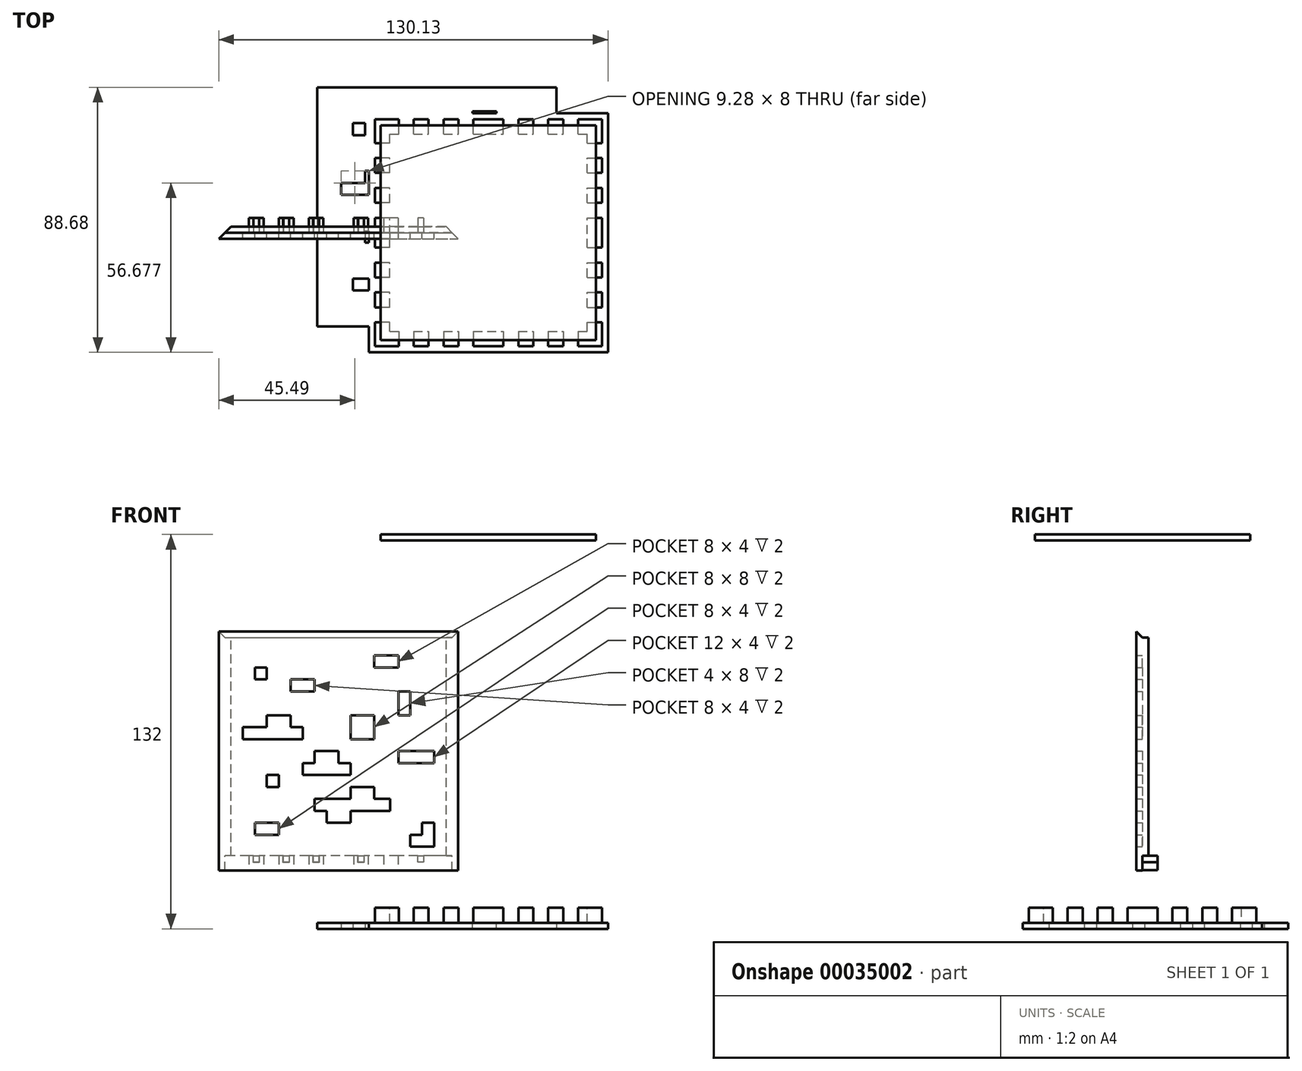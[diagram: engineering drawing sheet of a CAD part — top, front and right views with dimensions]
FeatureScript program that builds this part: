
annotation { "Feature Type Name" : "Feature", "Feature Type Description" : "" }
export const myFeature = defineFeature(function(context is Context, id is Id, definition is map)
    precondition{}
    {
        {
            var Q0;
            Q0=qCreatedBy(makeId("Top.planeOp"),FACE);
            var sketch = newSketch(context, id + "F0", { "sketchPlane" : qUnion([Q0])});
            skLineSegment(sketch, "E0", {"start": v(-57.28, 48.68) * mm, "end": v(-57.28, -31.32) * mm});
            skLineSegment(sketch, "E1.1.0.0", {"start": v(-53.28, 48.68) * mm, "end": v(-53.28, -31.32) * mm, "construction": true});
            skLineSegment(sketch, "E1.2.0.0", {"start": v(-49.28, 48.68) * mm, "end": v(-49.28, -31.32) * mm, "construction": true});
            skLineSegment(sketch, "E1.3.0.0", {"start": v(-45.28, 48.68) * mm, "end": v(-45.28, -31.32) * mm, "construction": true});
            skLineSegment(sketch, "E1.4.0.0", {"start": v(-41.28, 48.68) * mm, "end": v(-41.28, -31.32) * mm, "construction": true});
            skLineSegment(sketch, "E1.5.0.0", {"start": v(-37.28, 48.68) * mm, "end": v(-37.28, -31.32) * mm, "construction": true});
            skLineSegment(sketch, "E1.6.0.0", {"start": v(-33.28, 48.68) * mm, "end": v(-33.28, -31.32) * mm, "construction": true});
            skLineSegment(sketch, "E1.7.0.0", {"start": v(-29.28, 48.68) * mm, "end": v(-29.28, -31.32) * mm, "construction": true});
            skLineSegment(sketch, "E1.8.0.0", {"start": v(-25.28, 48.68) * mm, "end": v(-25.28, -31.32) * mm, "construction": true});
            skLineSegment(sketch, "E1.9.0.0", {"start": v(-21.28, 48.68) * mm, "end": v(-21.28, -31.32) * mm, "construction": true});
            skLineSegment(sketch, "E1.10.0.0", {"start": v(-17.28, 48.68) * mm, "end": v(-17.28, -31.32) * mm, "construction": true});
            skLineSegment(sketch, "E1.11.0.0", {"start": v(-13.28, 48.68) * mm, "end": v(-13.28, -31.32) * mm, "construction": true});
            skLineSegment(sketch, "E1.12.0.0", {"start": v(-9.28, 48.68) * mm, "end": v(-9.28, -31.32) * mm, "construction": true});
            skLineSegment(sketch, "E1.13.0.0", {"start": v(-5.28, 48.68) * mm, "end": v(-5.28, -31.32) * mm, "construction": true});
            skLineSegment(sketch, "E1.14.0.0", {"start": v(-1.28, 48.68) * mm, "end": v(-1.28, -31.32) * mm, "construction": true});
            skLineSegment(sketch, "E1.15.0.0", {"start": v(2.72, 48.68) * mm, "end": v(2.72, -31.32) * mm, "construction": true});
            skLineSegment(sketch, "E1.16.0.0", {"start": v(6.72, 48.68) * mm, "end": v(6.72, -31.32) * mm, "construction": true});
            skLineSegment(sketch, "E1.17.0.0", {"start": v(10.72, 48.68) * mm, "end": v(10.72, -31.32) * mm, "construction": true});
            skLineSegment(sketch, "E1.18.0.0", {"start": v(14.72, 48.68) * mm, "end": v(14.72, -31.32) * mm, "construction": true});
            skLineSegment(sketch, "E1.19.0.0", {"start": v(18.72, 48.68) * mm, "end": v(18.72, -31.32) * mm, "construction": true});
            skLineSegment(sketch, "E1.direction1", {"start": v(-57.28, -31.32) * mm, "end": v(-53.28, -31.32) * mm, "construction": true});
            skLineSegment(sketch, "E2", {"start": v(-57.28, 48.68) * mm, "end": v(22.72, 48.68) * mm});
            skLineSegment(sketch, "E3.0.20.0", {"start": v(22.72, 48.68) * mm, "end": v(22.72, -31.32) * mm});
            skLineSegment(sketch, "E4.0.1.0", {"start": v(-57.28, 44.68) * mm, "end": v(22.72, 44.68) * mm, "construction": true});
            skLineSegment(sketch, "E4.0.2.0", {"start": v(-57.28, 40.68) * mm, "end": v(22.72, 40.68) * mm, "construction": true});
            skLineSegment(sketch, "E4.0.3.0", {"start": v(-57.28, 36.68) * mm, "end": v(22.72, 36.68) * mm, "construction": true});
            skLineSegment(sketch, "E4.0.4.0", {"start": v(-57.28, 32.68) * mm, "end": v(22.72, 32.68) * mm, "construction": true});
            skLineSegment(sketch, "E4.0.5.0", {"start": v(-57.28, 28.68) * mm, "end": v(22.72, 28.68) * mm, "construction": true});
            skLineSegment(sketch, "E4.0.6.0", {"start": v(-57.28, 24.68) * mm, "end": v(22.72, 24.68) * mm, "construction": true});
            skLineSegment(sketch, "E4.0.7.0", {"start": v(-57.28, 20.68) * mm, "end": v(22.72, 20.68) * mm, "construction": true});
            skLineSegment(sketch, "E4.0.8.0", {"start": v(-57.28, 16.68) * mm, "end": v(22.72, 16.68) * mm, "construction": true});
            skLineSegment(sketch, "E4.0.9.0", {"start": v(-57.28, 12.68) * mm, "end": v(22.72, 12.68) * mm, "construction": true});
            skLineSegment(sketch, "E4.0.10.0", {"start": v(-57.28, 8.68) * mm, "end": v(22.72, 8.68) * mm, "construction": true});
            skLineSegment(sketch, "E4.0.11.0", {"start": v(-57.28, 4.68) * mm, "end": v(22.72, 4.68) * mm, "construction": true});
            skLineSegment(sketch, "E4.0.12.0", {"start": v(-57.28, 0.68) * mm, "end": v(22.72, 0.68) * mm, "construction": true});
            skLineSegment(sketch, "E4.0.13.0", {"start": v(-57.28, -3.32) * mm, "end": v(22.72, -3.32) * mm, "construction": true});
            skLineSegment(sketch, "E4.0.14.0", {"start": v(-57.28, -7.32) * mm, "end": v(22.72, -7.32) * mm, "construction": true});
            skLineSegment(sketch, "E4.0.15.0", {"start": v(-57.28, -11.32) * mm, "end": v(22.72, -11.32) * mm, "construction": true});
            skLineSegment(sketch, "E4.0.16.0", {"start": v(-57.28, -15.32) * mm, "end": v(22.72, -15.32) * mm, "construction": true});
            skLineSegment(sketch, "E4.0.17.0", {"start": v(-57.28, -19.32) * mm, "end": v(22.72, -19.32) * mm, "construction": true});
            skLineSegment(sketch, "E4.0.18.0", {"start": v(-57.28, -23.32) * mm, "end": v(22.72, -23.32) * mm, "construction": true});
            skLineSegment(sketch, "E4.0.19.0", {"start": v(-57.28, -27.32) * mm, "end": v(22.72, -27.32) * mm, "construction": true});
            skLineSegment(sketch, "E4.0.20.0", {"start": v(-57.28, -31.32) * mm, "end": v(22.72, -31.32) * mm});
            skLineSegment(sketch, "E4.direction1", {"start": v(-57.28, 48.68) * mm, "end": v(-53.28, 48.68) * mm, "construction": true});
            skLineSegment(sketch, "E4.direction2", {"start": v(-57.28, 48.68) * mm, "end": v(-57.28, 44.68) * mm, "construction": true});
            skLineSegment(sketch, "E5.bottom", {"start": v(-45.28, 36.68) * mm, "end": v(-41.28, 36.68) * mm});
            skLineSegment(sketch, "E5.top", {"start": v(-45.28, 32.68) * mm, "end": v(-41.28, 32.68) * mm});
            skLineSegment(sketch, "E5.left", {"start": v(-45.28, 36.68) * mm, "end": v(-45.28, 32.68) * mm});
            skLineSegment(sketch, "E5.right", {"start": v(-41.28, 36.68) * mm, "end": v(-41.28, 32.68) * mm});
            skLineSegment(sketch, "E6.bottom", {"start": v(-33.28, 32.68) * mm, "end": v(-25.28, 32.68) * mm});
            skLineSegment(sketch, "E6.top", {"start": v(-33.28, 28.68) * mm, "end": v(-25.28, 28.68) * mm});
            skLineSegment(sketch, "E6.left", {"start": v(-33.28, 32.68) * mm, "end": v(-33.28, 28.68) * mm});
            skLineSegment(sketch, "E6.right", {"start": v(-25.28, 32.68) * mm, "end": v(-25.28, 28.68) * mm});
            skLineSegment(sketch, "E7.bottom", {"start": v(-5.28, 36.68) * mm, "end": v(2.72, 36.68) * mm});
            skLineSegment(sketch, "E7.top", {"start": v(-5.28, 40.68) * mm, "end": v(2.72, 40.68) * mm});
            skLineSegment(sketch, "E7.left", {"start": v(-5.28, 36.68) * mm, "end": v(-5.28, 40.68) * mm});
            skLineSegment(sketch, "E7.right", {"start": v(2.72, 36.68) * mm, "end": v(2.72, 40.68) * mm});
            skPoint(sketch, "E8.firstSnap0", {"position": v(-17.28, 20.68) * mm});
            skLineSegment(sketch, "E8.bottom", {"start": v(-41.28, 20.68) * mm, "end": v(-33.28, 20.68) * mm});
            skLineSegment(sketch, "E8.top", {"start": v(-41.28, 16.68) * mm, "end": v(-33.28, 16.68) * mm});
            skLineSegment(sketch, "E8.left", {"start": v(-41.28, 20.68) * mm, "end": v(-41.28, 16.68) * mm});
            skLineSegment(sketch, "E8.right", {"start": v(-33.28, 20.68) * mm, "end": v(-33.28, 16.68) * mm});
            skLineSegment(sketch, "E9.bottom", {"start": v(-49.28, 16.68) * mm, "end": v(-29.28, 16.68) * mm});
            skLineSegment(sketch, "E9.top", {"start": v(-49.28, 12.68) * mm, "end": v(-29.28, 12.68) * mm});
            skLineSegment(sketch, "E9.left", {"start": v(-49.28, 16.68) * mm, "end": v(-49.28, 12.68) * mm});
            skLineSegment(sketch, "E9.right", {"start": v(-29.28, 16.68) * mm, "end": v(-29.28, 12.68) * mm});
            skLineSegment(sketch, "E10.bottom", {"start": v(-25.28, 8.68) * mm, "end": v(-17.28, 8.68) * mm});
            skLineSegment(sketch, "E10.top", {"start": v(-25.28, 4.68) * mm, "end": v(-17.28, 4.68) * mm});
            skLineSegment(sketch, "E10.left", {"start": v(-25.28, 8.68) * mm, "end": v(-25.28, 4.68) * mm});
            skLineSegment(sketch, "E10.right", {"start": v(-17.28, 8.68) * mm, "end": v(-17.28, 4.68) * mm});
            skLineSegment(sketch, "E11.bottom", {"start": v(-29.28, 4.68) * mm, "end": v(-13.28, 4.68) * mm});
            skLineSegment(sketch, "E11.top", {"start": v(-29.28, 0.68) * mm, "end": v(-13.28, 0.68) * mm});
            skLineSegment(sketch, "E11.left", {"start": v(-29.28, 4.68) * mm, "end": v(-29.28, 0.68) * mm});
            skLineSegment(sketch, "E11.right", {"start": v(-13.28, 4.68) * mm, "end": v(-13.28, 0.68) * mm});
            skLineSegment(sketch, "E12.bottom", {"start": v(-41.28, 0.68) * mm, "end": v(-37.28, 0.68) * mm});
            skLineSegment(sketch, "E12.top", {"start": v(-41.28, -3.32) * mm, "end": v(-37.28, -3.32) * mm});
            skLineSegment(sketch, "E12.left", {"start": v(-41.28, 0.68) * mm, "end": v(-41.28, -3.32) * mm});
            skLineSegment(sketch, "E12.right", {"start": v(-37.28, 0.68) * mm, "end": v(-37.28, -3.32) * mm});
            skLineSegment(sketch, "E13.bottom", {"start": v(-13.28, 12.68) * mm, "end": v(-5.28, 12.68) * mm});
            skLineSegment(sketch, "E13.top", {"start": v(-13.28, 20.68) * mm, "end": v(-5.28, 20.68) * mm});
            skLineSegment(sketch, "E13.left", {"start": v(-13.28, 12.68) * mm, "end": v(-13.28, 20.68) * mm});
            skLineSegment(sketch, "E13.right", {"start": v(-5.28, 12.68) * mm, "end": v(-5.28, 20.68) * mm});
            skLineSegment(sketch, "E14.bottom", {"start": v(2.72, 28.68) * mm, "end": v(6.72, 28.68) * mm});
            skLineSegment(sketch, "E14.top", {"start": v(2.72, 20.68) * mm, "end": v(6.72, 20.68) * mm});
            skLineSegment(sketch, "E14.left", {"start": v(2.72, 28.68) * mm, "end": v(2.72, 20.68) * mm});
            skLineSegment(sketch, "E14.right", {"start": v(6.72, 28.68) * mm, "end": v(6.72, 20.68) * mm});
            skLineSegment(sketch, "E15.bottom", {"start": v(-13.28, -3.32) * mm, "end": v(-5.28, -3.32) * mm});
            skLineSegment(sketch, "E15.top", {"start": v(-13.28, -7.32) * mm, "end": v(-5.28, -7.32) * mm});
            skLineSegment(sketch, "E15.left", {"start": v(-13.28, -3.32) * mm, "end": v(-13.28, -7.32) * mm});
            skLineSegment(sketch, "E15.right", {"start": v(-5.28, -3.32) * mm, "end": v(-5.28, -7.32) * mm});
            skLineSegment(sketch, "E16.bottom", {"start": v(0, -7.32) * mm, "end": v(-25.28, -7.32) * mm});
            skLineSegment(sketch, "E16.top", {"start": v(0, -11.32) * mm, "end": v(-25.28, -11.32) * mm});
            skLineSegment(sketch, "E16.left", {"start": v(0, -7.32) * mm, "end": v(0, -11.32) * mm});
            skLineSegment(sketch, "E16.right", {"start": v(-25.28, -7.32) * mm, "end": v(-25.28, -11.32) * mm});
            skLineSegment(sketch, "E17.bottom", {"start": v(-21.28, -11.32) * mm, "end": v(-13.28, -11.32) * mm});
            skLineSegment(sketch, "E17.top", {"start": v(-21.28, -15.32) * mm, "end": v(-13.28, -15.32) * mm});
            skLineSegment(sketch, "E17.left", {"start": v(-21.28, -11.32) * mm, "end": v(-21.28, -15.32) * mm});
            skLineSegment(sketch, "E17.right", {"start": v(-13.28, -11.32) * mm, "end": v(-13.28, -15.32) * mm});
            skLineSegment(sketch, "E18.bottom", {"start": v(-37.28, -15.32) * mm, "end": v(-45.28, -15.32) * mm});
            skLineSegment(sketch, "E18.top", {"start": v(-37.28, -19.32) * mm, "end": v(-45.28, -19.32) * mm});
            skLineSegment(sketch, "E18.left", {"start": v(-37.28, -15.32) * mm, "end": v(-37.28, -19.32) * mm});
            skLineSegment(sketch, "E18.right", {"start": v(-45.28, -15.32) * mm, "end": v(-45.28, -19.32) * mm});
            skLineSegment(sketch, "E19.bottom", {"start": v(6.72, -23.32) * mm, "end": v(14.72, -23.32) * mm});
            skLineSegment(sketch, "E19.top", {"start": v(6.72, -19.32) * mm, "end": v(14.72, -19.32) * mm});
            skLineSegment(sketch, "E19.left", {"start": v(6.72, -23.32) * mm, "end": v(6.72, -19.32) * mm});
            skLineSegment(sketch, "E19.right", {"start": v(14.72, -23.32) * mm, "end": v(14.72, -19.32) * mm});
            skLineSegment(sketch, "E20.bottom", {"start": v(10.72, -15.32) * mm, "end": v(14.72, -15.32) * mm});
            skLineSegment(sketch, "E20.top", {"start": v(10.72, -19.32) * mm, "end": v(14.72, -19.32) * mm});
            skLineSegment(sketch, "E20.left", {"start": v(10.72, -15.32) * mm, "end": v(10.72, -19.32) * mm});
            skLineSegment(sketch, "E20.right", {"start": v(14.72, -15.32) * mm, "end": v(14.72, -19.32) * mm});
            skLineSegment(sketch, "E21.bottom", {"start": v(2.72, 4.68) * mm, "end": v(14.72, 4.68) * mm});
            skLineSegment(sketch, "E21.top", {"start": v(2.72, 8.68) * mm, "end": v(14.72, 8.68) * mm});
            skLineSegment(sketch, "E21.left", {"start": v(2.72, 4.68) * mm, "end": v(2.72, 8.68) * mm});
            skLineSegment(sketch, "E21.right", {"start": v(14.72, 4.68) * mm, "end": v(14.72, 8.68) * mm});
            skSolve(sketch);
        }
        {
            var Q0;
            Q0=makeQuery(id+"F0.imprint","IMPRINT",FACE,{"disambiguationData":[TD([[makeQuery(id+"F0.imprint","IMPRINT",EDGE,{"derivedFrom":sQuery(id+"F0.wireOp",EDGE,"E0")}),1.0]])]});
            extrude(context, id + "F1", {"entities" : qUnion([Q0]), "depth" : 2 * mm});
        }
        {
            var Q0;
            Q0=qCreatedBy(makeId("Top.planeOp"),FACE);
            var sketch = newSketch(context, id + "F2", { "sketchPlane" : qUnion([Q0])});
            skLineSegment(sketch, "E22.bottom", {"start": v(40, 40) * mm, "end": v(-40, 40) * mm});
            skLineSegment(sketch, "E22.top", {"start": v(40, -40) * mm, "end": v(-40, -40) * mm});
            skLineSegment(sketch, "E22.left", {"start": v(40, 40) * mm, "end": v(40, -40) * mm});
            skLineSegment(sketch, "E22.right", {"start": v(-40, 40) * mm, "end": v(-40, -40) * mm});
            skPoint(sketch, "E22.middle", {"position": v(0, 0) * mm});
            skSolve(sketch);
        }
        {
            var Q0;
            Q0=makeQuery(id+"F2.imprint","IMPRINT",FACE,{"disambiguationData":[TD([[makeQuery(id+"F2.imprint","IMPRINT",EDGE,{"derivedFrom":sQuery(id+"F2.wireOp",EDGE,"E22.bottom")}),1.0]])]});
            extrude(context, id + "F3", {"entities" : qUnion([Q0]), "depth" : 2 * mm});
        }
        {
            var Q0;
            Q0=makeQuery(id+"F3.opExtrude","CAP_FACE",FACE,{"disambiguationData":[OSD([sQuery(id+"F2.wireOp",EDGE,"E22.bottom"),sQuery(id+"F2.wireOp",EDGE,"E22.top"),sQuery(id+"F2.wireOp",EDGE,"E22.left"),sQuery(id+"F2.wireOp",EDGE,"E22.right")])],"isStart":false});
            var sketch = newSketch(context, id + "F4", { "sketchPlane" : qUnion([Q0])});
            skLineSegment(sketch, "E23.bottom", {"start": v(38, 38) * mm, "end": v(-38, 38) * mm});
            skLineSegment(sketch, "E23.top", {"start": v(38, -38) * mm, "end": v(-38, -38) * mm});
            skLineSegment(sketch, "E23.left", {"start": v(38, 38) * mm, "end": v(38, -38) * mm});
            skLineSegment(sketch, "E23.right", {"start": v(-38, 38) * mm, "end": v(-38, -38) * mm});
            skPoint(sketch, "E23.middle", {"position": v(0, 0) * mm});
            skLineSegment(sketch, "E24.bottom", {"start": v(-33, -33) * mm, "end": v(33, -33) * mm});
            skLineSegment(sketch, "E24.top", {"start": v(-33, 33) * mm, "end": v(33, 33) * mm});
            skLineSegment(sketch, "E24.left", {"start": v(-33, -33) * mm, "end": v(-33, 33) * mm});
            skLineSegment(sketch, "E24.right", {"start": v(33, -33) * mm, "end": v(33, 33) * mm});
            skSolve(sketch);
        }
        {
            var Q0;
            Q0=makeQuery(id+"F4.imprint","IMPRINT",FACE,{"disambiguationData":[TD([[makeQuery(id+"F4.imprint","IMPRINT",EDGE,{"derivedFrom":sQuery(id+"F4.wireOp",EDGE,"E23.bottom")}),1.0]])]});
            extrude(context, id + "F5", {"entities" : qUnion([Q0]), "operationType" : NewBodyOperationType.ADD, "depth" : 5 * mm});
        }
        {
            var Q0;
            Q0=makeQuery(id+"F5.opExtrude","CAP_FACE",FACE,{"disambiguationData":[OSD([sQuery(id+"F4.wireOp",EDGE,"E23.bottom"),sQuery(id+"F4.wireOp",EDGE,"E23.top"),sQuery(id+"F4.wireOp",EDGE,"E23.left"),sQuery(id+"F4.wireOp",EDGE,"E23.right"),sQuery(id+"F4.wireOp",EDGE,"E24.bottom"),sQuery(id+"F4.wireOp",EDGE,"E24.top"),sQuery(id+"F4.wireOp",EDGE,"E24.left"),sQuery(id+"F4.wireOp",EDGE,"E24.right")])],"isStart":false});
            var sketch = newSketch(context, id + "F6", { "sketchPlane" : qUnion([Q0])});
            skLineSegment(sketch, "E25", {"start": v(-33, 30) * mm, "end": v(-38, 30) * mm});
            skLineSegment(sketch, "E26.0.1.0", {"start": v(-33, 25) * mm, "end": v(-38, 25) * mm});
            skLineSegment(sketch, "E26.0.2.0", {"start": v(-33, 20) * mm, "end": v(-38, 20) * mm});
            skLineSegment(sketch, "E26.0.3.0", {"start": v(-33, 15) * mm, "end": v(-38, 15) * mm});
            skLineSegment(sketch, "E26.0.4.0", {"start": v(-33, 10) * mm, "end": v(-38, 10) * mm});
            skLineSegment(sketch, "E26.0.5.0", {"start": v(-33, 5) * mm, "end": v(-38, 5) * mm});
            skLineSegment(sketch, "E26.0.6.0", {"start": v(-33, 0) * mm, "end": v(-38, 0) * mm});
            skLineSegment(sketch, "E26.direction1", {"start": v(-38, 30) * mm, "end": v(-13, 30) * mm, "construction": true});
            skLineSegment(sketch, "E26.direction2", {"start": v(-38, 30) * mm, "end": v(-38, 25) * mm, "construction": true});
            skLineSegment(sketch, "E27.0.0.7", {"start": v(-33, -5) * mm, "end": v(-38, -5) * mm});
            skLineSegment(sketch, "E27.0.0.8", {"start": v(-33, -10) * mm, "end": v(-38, -10) * mm});
            skLineSegment(sketch, "E27.0.0.9", {"start": v(-33, -15) * mm, "end": v(-38, -15) * mm});
            skLineSegment(sketch, "E27.0.0.10", {"start": v(-33, -20) * mm, "end": v(-38, -20) * mm});
            skLineSegment(sketch, "E27.0.0.11", {"start": v(-33, -25) * mm, "end": v(-38, -25) * mm});
            skLineSegment(sketch, "E28.0.0.12", {"start": v(-33, -30) * mm, "end": v(-38, -30) * mm});
            skLineSegment(sketch, "E29", {"start": v(0, 0) * mm, "end": v(0, 8.43) * mm, "construction": true});
            skLineSegment(sketch, "E30.MirrorCS", {"start": v(33, -30) * mm, "end": v(38, -30) * mm});
            skLineSegment(sketch, "E31.MirrorCS", {"start": v(33, -25) * mm, "end": v(38, -25) * mm});
            skLineSegment(sketch, "E32.MirrorCS", {"start": v(33, -20) * mm, "end": v(38, -20) * mm});
            skLineSegment(sketch, "E33.MirrorCS", {"start": v(33, -15) * mm, "end": v(38, -15) * mm});
            skLineSegment(sketch, "E34.MirrorCS", {"start": v(33, -10) * mm, "end": v(38, -10) * mm});
            skLineSegment(sketch, "E35.MirrorCS", {"start": v(33, -5) * mm, "end": v(38, -5) * mm});
            skLineSegment(sketch, "E36.MirrorCS", {"start": v(33, 0) * mm, "end": v(38, 0) * mm});
            skLineSegment(sketch, "E37.MirrorCS", {"start": v(33, 5) * mm, "end": v(38, 5) * mm});
            skLineSegment(sketch, "E38.MirrorCS", {"start": v(33, 10) * mm, "end": v(38, 10) * mm});
            skLineSegment(sketch, "E39.MirrorCS", {"start": v(33, 15) * mm, "end": v(38, 15) * mm});
            skLineSegment(sketch, "E40.MirrorCS", {"start": v(33, 20) * mm, "end": v(38, 20) * mm});
            skLineSegment(sketch, "E41.MirrorCS", {"start": v(33, 25) * mm, "end": v(38, 25) * mm});
            skLineSegment(sketch, "E42.MirrorCS", {"start": v(33, 30) * mm, "end": v(38, 30) * mm});
            skLineSegment(sketch, "E43", {"start": v(-30, -33) * mm, "end": v(-30, -38) * mm});
            skLineSegment(sketch, "E44.1.0.0", {"start": v(-25, -33) * mm, "end": v(-25, -38) * mm});
            skLineSegment(sketch, "E44.2.0.0", {"start": v(-20, -33) * mm, "end": v(-20, -38) * mm});
            skLineSegment(sketch, "E44.3.0.0", {"start": v(-15, -33) * mm, "end": v(-15, -38) * mm});
            skLineSegment(sketch, "E44.4.0.0", {"start": v(-10, -33) * mm, "end": v(-10, -38) * mm});
            skLineSegment(sketch, "E44.5.0.0", {"start": v(-5, -33) * mm, "end": v(-5, -38) * mm});
            skLineSegment(sketch, "E44.6.0.0", {"start": v(0, -33) * mm, "end": v(0, -38) * mm});
            skLineSegment(sketch, "E44.7.0.0", {"start": v(5, -33) * mm, "end": v(5, -38) * mm});
            skLineSegment(sketch, "E44.8.0.0", {"start": v(10, -33) * mm, "end": v(10, -38) * mm});
            skLineSegment(sketch, "E44.9.0.0", {"start": v(15, -33) * mm, "end": v(15, -38) * mm});
            skLineSegment(sketch, "E44.10.0.0", {"start": v(20, -33) * mm, "end": v(20, -38) * mm});
            skLineSegment(sketch, "E44.11.0.0", {"start": v(25, -33) * mm, "end": v(25, -38) * mm});
            skLineSegment(sketch, "E44.12.0.0", {"start": v(30, -33) * mm, "end": v(30, -38) * mm});
            skLineSegment(sketch, "E44.direction1", {"start": v(-30, -38) * mm, "end": v(-25, -38) * mm, "construction": true});
            skLineSegment(sketch, "E45", {"start": v(0, 0) * mm, "end": v(-14.9, 0) * mm, "construction": true});
            skLineSegment(sketch, "E46.MirrorCS", {"start": v(5, 33) * mm, "end": v(5, 38) * mm});
            skLineSegment(sketch, "E47.MirrorCS", {"start": v(-5, 33) * mm, "end": v(-5, 38) * mm});
            skLineSegment(sketch, "E48.MirrorCS", {"start": v(-15, 33) * mm, "end": v(-15, 38) * mm});
            skLineSegment(sketch, "E49.MirrorCS", {"start": v(0, 33) * mm, "end": v(0, 38) * mm});
            skLineSegment(sketch, "E50.MirrorCS", {"start": v(-10, 33) * mm, "end": v(-10, 38) * mm});
            skLineSegment(sketch, "E51.MirrorCS", {"start": v(-25, 33) * mm, "end": v(-25, 38) * mm});
            skLineSegment(sketch, "E52.MirrorCS", {"start": v(-30, 33) * mm, "end": v(-30, 38) * mm});
            skLineSegment(sketch, "E53.MirrorCS", {"start": v(-20, 33) * mm, "end": v(-20, 38) * mm});
            skLineSegment(sketch, "E54.MirrorCS", {"start": v(10, 33) * mm, "end": v(10, 38) * mm});
            skLineSegment(sketch, "E55.MirrorCS", {"start": v(20, 33) * mm, "end": v(20, 38) * mm});
            skLineSegment(sketch, "E56.MirrorCS", {"start": v(-30, 38) * mm, "end": v(-25, 38) * mm, "construction": true});
            skLineSegment(sketch, "E57.MirrorCS", {"start": v(25, 33) * mm, "end": v(25, 38) * mm});
            skLineSegment(sketch, "E58.MirrorCS", {"start": v(15, 33) * mm, "end": v(15, 38) * mm});
            skLineSegment(sketch, "E59.MirrorCS", {"start": v(30, 33) * mm, "end": v(30, 38) * mm});
            skSolve(sketch);
        }
        {
            var Q0;
            {var subQ0=sQuery(id+"F6.wireOp",EDGE,"E27.0.0.11");Q0=makeQuery(id+"F6.imprint","IMPRINT",FACE,{"disambiguationData":[TD([[makeQuery(id+"F6.imprint","IMPRINT",EDGE,{"derivedFrom":subQ0}),1.0]])]});}
            var Q1;
            {var subQ0=sQuery(id+"F6.wireOp",EDGE,"E27.0.0.9");Q1=makeQuery(id+"F6.imprint","IMPRINT",FACE,{"disambiguationData":[TD([[makeQuery(id+"F6.imprint","IMPRINT",EDGE,{"derivedFrom":subQ0}),1.0]])]});}
            var Q2;
            {var subQ0=sQuery(id+"F6.wireOp",EDGE,"E27.0.0.7");Q2=makeQuery(id+"F6.imprint","IMPRINT",FACE,{"disambiguationData":[TD([[makeQuery(id+"F6.imprint","IMPRINT",EDGE,{"derivedFrom":subQ0}),1.0]])]});}
            var Q3;
            {var subQ0=sQuery(id+"F6.wireOp",EDGE,"E25");Q3=makeQuery(id+"F6.imprint","IMPRINT",FACE,{"disambiguationData":[TD([[makeQuery(id+"F6.imprint","IMPRINT",EDGE,{"derivedFrom":subQ0}),1.0]])]});}
            var Q4;
            {var subQ0=sQuery(id+"F6.wireOp",EDGE,"E26.0.2.0");Q4=makeQuery(id+"F6.imprint","IMPRINT",FACE,{"disambiguationData":[TD([[makeQuery(id+"F6.imprint","IMPRINT",EDGE,{"derivedFrom":subQ0}),1.0]])]});}
            var Q5;
            {var subQ0=sQuery(id+"F6.wireOp",EDGE,"E26.0.4.0");Q5=makeQuery(id+"F6.imprint","IMPRINT",FACE,{"disambiguationData":[TD([[makeQuery(id+"F6.imprint","IMPRINT",EDGE,{"derivedFrom":subQ0}),1.0]])]});}
            var Q6;
            {var subQ0=sQuery(id+"F6.wireOp",EDGE,"E30.MirrorCS");Q6=makeQuery(id+"F6.imprint","IMPRINT",FACE,{"disambiguationData":[TD([[makeQuery(id+"F6.imprint","IMPRINT",EDGE,{"derivedFrom":subQ0}),1.0]])]});}
            var Q7;
            {var subQ0=sQuery(id+"F6.wireOp",EDGE,"E32.MirrorCS");Q7=makeQuery(id+"F6.imprint","IMPRINT",FACE,{"disambiguationData":[TD([[makeQuery(id+"F6.imprint","IMPRINT",EDGE,{"derivedFrom":subQ0}),1.0]])]});}
            var Q8;
            {var subQ0=sQuery(id+"F6.wireOp",EDGE,"E34.MirrorCS");Q8=makeQuery(id+"F6.imprint","IMPRINT",FACE,{"disambiguationData":[TD([[makeQuery(id+"F6.imprint","IMPRINT",EDGE,{"derivedFrom":subQ0}),1.0]])]});}
            var Q9;
            {var subQ0=sQuery(id+"F6.wireOp",EDGE,"E41.MirrorCS");Q9=makeQuery(id+"F6.imprint","IMPRINT",FACE,{"disambiguationData":[TD([[makeQuery(id+"F6.imprint","IMPRINT",EDGE,{"derivedFrom":subQ0}),1.0]])]});}
            var Q10;
            {var subQ0=sQuery(id+"F6.wireOp",EDGE,"E39.MirrorCS");Q10=makeQuery(id+"F6.imprint","IMPRINT",FACE,{"disambiguationData":[TD([[makeQuery(id+"F6.imprint","IMPRINT",EDGE,{"derivedFrom":subQ0}),1.0]])]});}
            var Q11;
            {var subQ0=sQuery(id+"F6.wireOp",EDGE,"E37.MirrorCS");Q11=makeQuery(id+"F6.imprint","IMPRINT",FACE,{"disambiguationData":[TD([[makeQuery(id+"F6.imprint","IMPRINT",EDGE,{"derivedFrom":subQ0}),1.0]])]});}
            var Q12;
            {var subQ0=sQuery(id+"F6.wireOp",EDGE,"E51.MirrorCS");Q12=makeQuery(id+"F6.imprint","IMPRINT",FACE,{"disambiguationData":[TD([[makeQuery(id+"F6.imprint","IMPRINT",EDGE,{"derivedFrom":subQ0}),1.0]])]});}
            var Q13;
            {var subQ0=sQuery(id+"F6.wireOp",EDGE,"E48.MirrorCS");Q13=makeQuery(id+"F6.imprint","IMPRINT",FACE,{"disambiguationData":[TD([[makeQuery(id+"F6.imprint","IMPRINT",EDGE,{"derivedFrom":subQ0}),1.0]])]});}
            var Q14;
            {var subQ0=sQuery(id+"F6.wireOp",EDGE,"E57.MirrorCS");Q14=makeQuery(id+"F6.imprint","IMPRINT",FACE,{"disambiguationData":[TD([[makeQuery(id+"F6.imprint","IMPRINT",EDGE,{"derivedFrom":subQ0}),-1.0]])]});}
            var Q15;
            {var subQ0=sQuery(id+"F6.wireOp",EDGE,"E55.MirrorCS");Q15=makeQuery(id+"F6.imprint","IMPRINT",FACE,{"disambiguationData":[TD([[makeQuery(id+"F6.imprint","IMPRINT",EDGE,{"derivedFrom":subQ0}),1.0]])]});}
            var Q16;
            {var subQ0=sQuery(id+"F6.wireOp",EDGE,"E46.MirrorCS");Q16=makeQuery(id+"F6.imprint","IMPRINT",FACE,{"disambiguationData":[TD([[makeQuery(id+"F6.imprint","IMPRINT",EDGE,{"derivedFrom":subQ0}),-1.0]])]});}
            var Q17;
            {var subQ0=sQuery(id+"F6.wireOp",EDGE,"E47.MirrorCS");Q17=makeQuery(id+"F6.imprint","IMPRINT",FACE,{"disambiguationData":[TD([[makeQuery(id+"F6.imprint","IMPRINT",EDGE,{"derivedFrom":subQ0}),1.0]])]});}
            var Q18;
            {var subQ0=sQuery(id+"F6.wireOp",EDGE,"E43");Q18=makeQuery(id+"F6.imprint","IMPRINT",FACE,{"disambiguationData":[TD([[makeQuery(id+"F6.imprint","IMPRINT",EDGE,{"derivedFrom":subQ0}),1.0]])]});}
            var Q19;
            {var subQ0=sQuery(id+"F6.wireOp",EDGE,"E44.2.0.0");Q19=makeQuery(id+"F6.imprint","IMPRINT",FACE,{"disambiguationData":[TD([[makeQuery(id+"F6.imprint","IMPRINT",EDGE,{"derivedFrom":subQ0}),1.0]])]});}
            var Q20;
            {var subQ0=sQuery(id+"F6.wireOp",EDGE,"E44.4.0.0");Q20=makeQuery(id+"F6.imprint","IMPRINT",FACE,{"disambiguationData":[TD([[makeQuery(id+"F6.imprint","IMPRINT",EDGE,{"derivedFrom":subQ0}),1.0]])]});}
            var Q21;
            {var subQ0=sQuery(id+"F6.wireOp",EDGE,"E44.11.0.0");Q21=makeQuery(id+"F6.imprint","IMPRINT",FACE,{"disambiguationData":[TD([[makeQuery(id+"F6.imprint","IMPRINT",EDGE,{"derivedFrom":subQ0}),1.0]])]});}
            var Q22;
            {var subQ0=sQuery(id+"F6.wireOp",EDGE,"E44.9.0.0");Q22=makeQuery(id+"F6.imprint","IMPRINT",FACE,{"disambiguationData":[TD([[makeQuery(id+"F6.imprint","IMPRINT",EDGE,{"derivedFrom":subQ0}),1.0]])]});}
            var Q23;
            {var subQ0=sQuery(id+"F6.wireOp",EDGE,"E44.7.0.0");Q23=makeQuery(id+"F6.imprint","IMPRINT",FACE,{"disambiguationData":[TD([[makeQuery(id+"F6.imprint","IMPRINT",EDGE,{"derivedFrom":subQ0}),1.0]])]});}
            extrude(context, id + "F7", {"entities" : qUnion([Q0, Q1, Q2, Q3, Q4, Q5, Q6, Q7, Q8, Q9, Q10, Q11, Q12, Q13, Q14, Q15, Q16, Q17, Q18, Q19, Q20, Q21, Q22, Q23]), "operationType" : NewBodyOperationType.REMOVE, "oppositeDirection" : true, "depth" : 5 * mm});
        }
        {
            var Q0;
            Q0=qCreatedBy(makeId("Front.planeOp"),FACE);
            var sketch = newSketch(context, id + "F8", { "sketchPlane" : qUnion([Q0])});
            skLineSegment(sketch, "E60", {"start": v(-90.13, 99.5) * mm, "end": v(-90.13, 19.5) * mm});
            skLineSegment(sketch, "E61.1.0.0", {"start": v(-86.13, 99.5) * mm, "end": v(-86.13, 19.5) * mm, "construction": true});
            skLineSegment(sketch, "E61.2.0.0", {"start": v(-82.13, 99.5) * mm, "end": v(-82.13, 19.5) * mm, "construction": true});
            skLineSegment(sketch, "E61.3.0.0", {"start": v(-78.13, 99.5) * mm, "end": v(-78.13, 19.5) * mm, "construction": true});
            skLineSegment(sketch, "E61.4.0.0", {"start": v(-74.13, 99.5) * mm, "end": v(-74.13, 19.5) * mm, "construction": true});
            skLineSegment(sketch, "E61.5.0.0", {"start": v(-70.13, 99.5) * mm, "end": v(-70.13, 19.5) * mm, "construction": true});
            skLineSegment(sketch, "E61.6.0.0", {"start": v(-66.13, 99.5) * mm, "end": v(-66.13, 19.5) * mm, "construction": true});
            skLineSegment(sketch, "E61.7.0.0", {"start": v(-62.13, 99.5) * mm, "end": v(-62.13, 19.5) * mm, "construction": true});
            skLineSegment(sketch, "E61.8.0.0", {"start": v(-58.13, 99.5) * mm, "end": v(-58.13, 19.5) * mm, "construction": true});
            skLineSegment(sketch, "E61.9.0.0", {"start": v(-54.13, 99.5) * mm, "end": v(-54.13, 19.5) * mm, "construction": true});
            skLineSegment(sketch, "E61.10.0.0", {"start": v(-50.13, 99.5) * mm, "end": v(-50.13, 19.5) * mm, "construction": true});
            skLineSegment(sketch, "E61.11.0.0", {"start": v(-46.13, 99.5) * mm, "end": v(-46.13, 19.5) * mm, "construction": true});
            skLineSegment(sketch, "E61.12.0.0", {"start": v(-42.13, 99.5) * mm, "end": v(-42.13, 19.5) * mm, "construction": true});
            skLineSegment(sketch, "E61.13.0.0", {"start": v(-38.13, 99.5) * mm, "end": v(-38.13, 19.5) * mm, "construction": true});
            skLineSegment(sketch, "E61.14.0.0", {"start": v(-34.13, 99.5) * mm, "end": v(-34.13, 19.5) * mm, "construction": true});
            skLineSegment(sketch, "E61.15.0.0", {"start": v(-30.13, 99.5) * mm, "end": v(-30.13, 19.5) * mm, "construction": true});
            skLineSegment(sketch, "E61.16.0.0", {"start": v(-26.13, 99.5) * mm, "end": v(-26.13, 19.5) * mm, "construction": true});
            skLineSegment(sketch, "E61.17.0.0", {"start": v(-22.13, 99.5) * mm, "end": v(-22.13, 19.5) * mm, "construction": true});
            skLineSegment(sketch, "E61.18.0.0", {"start": v(-18.13, 99.5) * mm, "end": v(-18.13, 19.5) * mm, "construction": true});
            skLineSegment(sketch, "E61.19.0.0", {"start": v(-14.13, 99.5) * mm, "end": v(-14.13, 19.5) * mm, "construction": true});
            skLineSegment(sketch, "E61.direction1", {"start": v(-90.13, 19.5) * mm, "end": v(-86.13, 19.5) * mm, "construction": true});
            skLineSegment(sketch, "E62", {"start": v(-90.13, 99.5) * mm, "end": v(-10.13, 99.5) * mm});
            skLineSegment(sketch, "E63.0.20.0", {"start": v(-10.13, 99.5) * mm, "end": v(-10.13, 19.5) * mm});
            skLineSegment(sketch, "E64.0.1.0", {"start": v(-90.13, 95.5) * mm, "end": v(-10.13, 95.5) * mm, "construction": true});
            skLineSegment(sketch, "E64.0.2.0", {"start": v(-90.13, 91.5) * mm, "end": v(-10.13, 91.5) * mm, "construction": true});
            skLineSegment(sketch, "E64.0.3.0", {"start": v(-90.13, 87.5) * mm, "end": v(-10.13, 87.5) * mm, "construction": true});
            skLineSegment(sketch, "E64.0.4.0", {"start": v(-90.13, 83.5) * mm, "end": v(-10.13, 83.5) * mm, "construction": true});
            skLineSegment(sketch, "E64.0.5.0", {"start": v(-90.13, 79.5) * mm, "end": v(-10.13, 79.5) * mm, "construction": true});
            skLineSegment(sketch, "E64.0.6.0", {"start": v(-90.13, 75.5) * mm, "end": v(-10.13, 75.5) * mm, "construction": true});
            skLineSegment(sketch, "E64.0.7.0", {"start": v(-90.13, 71.5) * mm, "end": v(-10.13, 71.5) * mm, "construction": true});
            skLineSegment(sketch, "E64.0.8.0", {"start": v(-90.13, 67.5) * mm, "end": v(-10.13, 67.5) * mm, "construction": true});
            skLineSegment(sketch, "E64.0.9.0", {"start": v(-90.13, 63.5) * mm, "end": v(-10.13, 63.5) * mm, "construction": true});
            skLineSegment(sketch, "E64.0.10.0", {"start": v(-90.13, 59.5) * mm, "end": v(-10.13, 59.5) * mm, "construction": true});
            skLineSegment(sketch, "E64.0.11.0", {"start": v(-90.13, 55.5) * mm, "end": v(-10.13, 55.5) * mm, "construction": true});
            skLineSegment(sketch, "E64.0.12.0", {"start": v(-90.13, 51.5) * mm, "end": v(-10.13, 51.5) * mm, "construction": true});
            skLineSegment(sketch, "E64.0.13.0", {"start": v(-90.13, 47.5) * mm, "end": v(-10.13, 47.5) * mm, "construction": true});
            skLineSegment(sketch, "E64.0.14.0", {"start": v(-90.13, 43.5) * mm, "end": v(-10.13, 43.5) * mm, "construction": true});
            skLineSegment(sketch, "E64.0.15.0", {"start": v(-90.13, 39.5) * mm, "end": v(-10.13, 39.5) * mm, "construction": true});
            skLineSegment(sketch, "E64.0.16.0", {"start": v(-90.13, 35.5) * mm, "end": v(-10.13, 35.5) * mm, "construction": true});
            skLineSegment(sketch, "E64.0.17.0", {"start": v(-90.13, 31.5) * mm, "end": v(-10.13, 31.5) * mm, "construction": true});
            skLineSegment(sketch, "E64.0.18.0", {"start": v(-90.13, 27.5) * mm, "end": v(-10.13, 27.5) * mm, "construction": true});
            skLineSegment(sketch, "E64.0.19.0", {"start": v(-90.13, 23.5) * mm, "end": v(-10.13, 23.5) * mm, "construction": true});
            skLineSegment(sketch, "E64.0.20.0", {"start": v(-90.13, 19.5) * mm, "end": v(-10.13, 19.5) * mm});
            skLineSegment(sketch, "E64.direction1", {"start": v(-90.13, 99.5) * mm, "end": v(-86.13, 99.5) * mm, "construction": true});
            skLineSegment(sketch, "E64.direction2", {"start": v(-90.13, 99.5) * mm, "end": v(-90.13, 95.5) * mm, "construction": true});
            skLineSegment(sketch, "E65.bottom", {"start": v(-78.13, 87.5) * mm, "end": v(-74.13, 87.5) * mm});
            skLineSegment(sketch, "E65.top", {"start": v(-78.13, 83.5) * mm, "end": v(-74.13, 83.5) * mm});
            skLineSegment(sketch, "E65.left", {"start": v(-78.13, 87.5) * mm, "end": v(-78.13, 83.5) * mm});
            skLineSegment(sketch, "E65.right", {"start": v(-74.13, 87.5) * mm, "end": v(-74.13, 83.5) * mm});
            skLineSegment(sketch, "E66.bottom", {"start": v(-66.13, 83.5) * mm, "end": v(-58.13, 83.5) * mm});
            skLineSegment(sketch, "E66.top", {"start": v(-66.13, 79.5) * mm, "end": v(-58.13, 79.5) * mm});
            skLineSegment(sketch, "E66.left", {"start": v(-66.13, 83.5) * mm, "end": v(-66.13, 79.5) * mm});
            skLineSegment(sketch, "E66.right", {"start": v(-58.13, 83.5) * mm, "end": v(-58.13, 79.5) * mm});
            skLineSegment(sketch, "E67.bottom", {"start": v(-38.13, 87.5) * mm, "end": v(-30.13, 87.5) * mm});
            skLineSegment(sketch, "E67.top", {"start": v(-38.13, 91.5) * mm, "end": v(-30.13, 91.5) * mm});
            skLineSegment(sketch, "E67.left", {"start": v(-38.13, 87.5) * mm, "end": v(-38.13, 91.5) * mm});
            skLineSegment(sketch, "E67.right", {"start": v(-30.13, 87.5) * mm, "end": v(-30.13, 91.5) * mm});
            skPoint(sketch, "E68.firstSnap0", {"position": v(-50.13, 71.5) * mm});
            skLineSegment(sketch, "E68.bottom", {"start": v(-74.13, 71.5) * mm, "end": v(-66.13, 71.5) * mm});
            skLineSegment(sketch, "E68.top", {"start": v(-74.13, 67.5) * mm, "end": v(-66.13, 67.5) * mm});
            skLineSegment(sketch, "E68.left", {"start": v(-74.13, 71.5) * mm, "end": v(-74.13, 67.5) * mm});
            skLineSegment(sketch, "E68.right", {"start": v(-66.13, 71.5) * mm, "end": v(-66.13, 67.5) * mm});
            skLineSegment(sketch, "E69.bottom", {"start": v(-82.13, 67.5) * mm, "end": v(-62.13, 67.5) * mm});
            skLineSegment(sketch, "E69.top", {"start": v(-82.13, 63.5) * mm, "end": v(-62.13, 63.5) * mm});
            skLineSegment(sketch, "E69.left", {"start": v(-82.13, 67.5) * mm, "end": v(-82.13, 63.5) * mm});
            skLineSegment(sketch, "E69.right", {"start": v(-62.13, 67.5) * mm, "end": v(-62.13, 63.5) * mm});
            skLineSegment(sketch, "E70.bottom", {"start": v(-58.13, 59.5) * mm, "end": v(-50.13, 59.5) * mm});
            skLineSegment(sketch, "E70.top", {"start": v(-58.13, 55.5) * mm, "end": v(-50.13, 55.5) * mm});
            skLineSegment(sketch, "E70.left", {"start": v(-58.13, 59.5) * mm, "end": v(-58.13, 55.5) * mm});
            skLineSegment(sketch, "E70.right", {"start": v(-50.13, 59.5) * mm, "end": v(-50.13, 55.5) * mm});
            skLineSegment(sketch, "E71.bottom", {"start": v(-62.13, 55.5) * mm, "end": v(-46.13, 55.5) * mm});
            skLineSegment(sketch, "E71.top", {"start": v(-62.13, 51.5) * mm, "end": v(-46.13, 51.5) * mm});
            skLineSegment(sketch, "E71.left", {"start": v(-62.13, 55.5) * mm, "end": v(-62.13, 51.5) * mm});
            skLineSegment(sketch, "E71.right", {"start": v(-46.13, 55.5) * mm, "end": v(-46.13, 51.5) * mm});
            skLineSegment(sketch, "E72.bottom", {"start": v(-74.13, 51.5) * mm, "end": v(-70.13, 51.5) * mm});
            skLineSegment(sketch, "E72.top", {"start": v(-74.13, 47.5) * mm, "end": v(-70.13, 47.5) * mm});
            skLineSegment(sketch, "E72.left", {"start": v(-74.13, 51.5) * mm, "end": v(-74.13, 47.5) * mm});
            skLineSegment(sketch, "E72.right", {"start": v(-70.13, 51.5) * mm, "end": v(-70.13, 47.5) * mm});
            skLineSegment(sketch, "E73.bottom", {"start": v(-46.13, 63.5) * mm, "end": v(-38.13, 63.5) * mm});
            skLineSegment(sketch, "E73.top", {"start": v(-46.13, 71.5) * mm, "end": v(-38.13, 71.5) * mm});
            skLineSegment(sketch, "E73.left", {"start": v(-46.13, 63.5) * mm, "end": v(-46.13, 71.5) * mm});
            skLineSegment(sketch, "E73.right", {"start": v(-38.13, 63.5) * mm, "end": v(-38.13, 71.5) * mm});
            skLineSegment(sketch, "E74.bottom", {"start": v(-30.13, 79.5) * mm, "end": v(-26.13, 79.5) * mm});
            skLineSegment(sketch, "E74.top", {"start": v(-30.13, 71.5) * mm, "end": v(-26.13, 71.5) * mm});
            skLineSegment(sketch, "E74.left", {"start": v(-30.13, 79.5) * mm, "end": v(-30.13, 71.5) * mm});
            skLineSegment(sketch, "E74.right", {"start": v(-26.13, 79.5) * mm, "end": v(-26.13, 71.5) * mm});
            skLineSegment(sketch, "E75.bottom", {"start": v(-46.13, 47.5) * mm, "end": v(-38.13, 47.5) * mm});
            skLineSegment(sketch, "E75.top", {"start": v(-46.13, 43.5) * mm, "end": v(-38.13, 43.5) * mm});
            skLineSegment(sketch, "E75.left", {"start": v(-46.13, 47.5) * mm, "end": v(-46.13, 43.5) * mm});
            skLineSegment(sketch, "E75.right", {"start": v(-38.13, 47.5) * mm, "end": v(-38.13, 43.5) * mm});
            skLineSegment(sketch, "E76.bottom", {"start": v(-32.85, 43.5) * mm, "end": v(-58.13, 43.5) * mm});
            skLineSegment(sketch, "E76.top", {"start": v(-32.85, 39.5) * mm, "end": v(-58.13, 39.5) * mm});
            skLineSegment(sketch, "E76.left", {"start": v(-32.85, 43.5) * mm, "end": v(-32.85, 39.5) * mm});
            skLineSegment(sketch, "E76.right", {"start": v(-58.13, 43.5) * mm, "end": v(-58.13, 39.5) * mm});
            skLineSegment(sketch, "E77.bottom", {"start": v(-54.13, 39.5) * mm, "end": v(-46.13, 39.5) * mm});
            skLineSegment(sketch, "E77.top", {"start": v(-54.13, 35.5) * mm, "end": v(-46.13, 35.5) * mm});
            skLineSegment(sketch, "E77.left", {"start": v(-54.13, 39.5) * mm, "end": v(-54.13, 35.5) * mm});
            skLineSegment(sketch, "E77.right", {"start": v(-46.13, 39.5) * mm, "end": v(-46.13, 35.5) * mm});
            skLineSegment(sketch, "E78.bottom", {"start": v(-70.13, 35.5) * mm, "end": v(-78.13, 35.5) * mm});
            skLineSegment(sketch, "E78.top", {"start": v(-70.13, 31.5) * mm, "end": v(-78.13, 31.5) * mm});
            skLineSegment(sketch, "E78.left", {"start": v(-70.13, 35.5) * mm, "end": v(-70.13, 31.5) * mm});
            skLineSegment(sketch, "E78.right", {"start": v(-78.13, 35.5) * mm, "end": v(-78.13, 31.5) * mm});
            skLineSegment(sketch, "E79.bottom", {"start": v(-26.13, 27.5) * mm, "end": v(-18.13, 27.5) * mm});
            skLineSegment(sketch, "E79.top", {"start": v(-26.13, 31.5) * mm, "end": v(-18.13, 31.5) * mm});
            skLineSegment(sketch, "E79.left", {"start": v(-26.13, 27.5) * mm, "end": v(-26.13, 31.5) * mm});
            skLineSegment(sketch, "E79.right", {"start": v(-18.13, 27.5) * mm, "end": v(-18.13, 31.5) * mm});
            skLineSegment(sketch, "E80.bottom", {"start": v(-22.13, 35.5) * mm, "end": v(-18.13, 35.5) * mm});
            skLineSegment(sketch, "E80.top", {"start": v(-22.13, 31.5) * mm, "end": v(-18.13, 31.5) * mm});
            skLineSegment(sketch, "E80.left", {"start": v(-22.13, 35.5) * mm, "end": v(-22.13, 31.5) * mm});
            skLineSegment(sketch, "E80.right", {"start": v(-18.13, 35.5) * mm, "end": v(-18.13, 31.5) * mm});
            skLineSegment(sketch, "E81.bottom", {"start": v(-30.13, 55.5) * mm, "end": v(-18.13, 55.5) * mm});
            skLineSegment(sketch, "E81.top", {"start": v(-30.13, 59.5) * mm, "end": v(-18.13, 59.5) * mm});
            skLineSegment(sketch, "E81.left", {"start": v(-30.13, 55.5) * mm, "end": v(-30.13, 59.5) * mm});
            skLineSegment(sketch, "E81.right", {"start": v(-18.13, 55.5) * mm, "end": v(-18.13, 59.5) * mm});
            skSolve(sketch);
        }
        {
            var Q0;
            Q0=makeQuery(id+"F8.imprint","IMPRINT",FACE,{"disambiguationData":[TD([[makeQuery(id+"F8.imprint","IMPRINT",EDGE,{"derivedFrom":sQuery(id+"F8.wireOp",EDGE,"E60")}),1.0]])]});
            extrude(context, id + "F9", {"entities" : qUnion([Q0]), "depth" : 2 * mm});
        }
        {
            var Q0;
            Q0=makeQuery(id+"F9.opExtrude","SWEPT_FACE",FACE,{"disambiguationData":[OSD([sQuery(id+"F8.wireOp",EDGE,"E63.0.20.0")])]});
            cPlane(context, id + "F10", {"entities" : qUnion([Q0]), "cplaneType" : CPlaneType.OFFSET, "offset" : 0 * mm, "width" : 150 * mm, "height" : 150 * mm});
        }
        {
            var Q0;
            Q0=makeQuery(id+"F9.opExtrude","SWEPT_FACE",FACE,{"disambiguationData":[OSD([sQuery(id+"F8.wireOp",EDGE,"E62")])]});
            cPlane(context, id + "F11", {"entities" : qUnion([Q0]), "cplaneType" : CPlaneType.OFFSET, "offset" : 0 * mm, "width" : 150 * mm, "height" : 150 * mm});
        }
        {
            var Q0;
            Q0=qCreatedBy(id+"F10.planeOp",FACE);
            var sketch = newSketch(context, id + "F12", { "sketchPlane" : qUnion([Q0])});
            skLineSegment(sketch, "E82", {"start": v(-2, 99.5) * mm, "end": v(0, 97.5) * mm});
            skLineSegment(sketch, "E83", {"start": v(-2, 99.5) * mm, "end": v(0, 99.5) * mm});
            skLineSegment(sketch, "E84", {"start": v(0, 99.5) * mm, "end": v(0, 97.5) * mm});
            skSolve(sketch);
        }
        {
            var Q0;
            Q0=makeQuery(id+"F12.imprint","IMPRINT",FACE,{"disambiguationData":[TD([[makeQuery(id+"F12.imprint","IMPRINT",EDGE,{"derivedFrom":sQuery(id+"F12.wireOp",EDGE,"E82")}),1.0]])]});
            extrude(context, id + "F13", {"entities" : qUnion([Q0]), "operationType" : NewBodyOperationType.REMOVE, "endBound" : BoundingType.UP_TO_NEXT, "oppositeDirection" : true, "depth" : 25 * mm});
        }
        {
            var Q0;
            Q0=qCreatedBy(id+"F11.planeOp",FACE);
            var sketch = newSketch(context, id + "F14", { "sketchPlane" : qUnion([Q0])});
            skLineSegment(sketch, "E85", {"start": v(-10.13, -2) * mm, "end": v(-12.13, 0) * mm});
            skLineSegment(sketch, "E86", {"start": v(-50.13, 0) * mm, "end": v(-50.13, -2) * mm, "construction": true});
            skLineSegment(sketch, "E87.MirrorCS", {"start": v(-90.13, -2) * mm, "end": v(-88.13, 0) * mm});
            skLineSegment(sketch, "E88", {"start": v(-12.13, 0) * mm, "end": v(-10.13, 0) * mm});
            skLineSegment(sketch, "E89", {"start": v(-10.13, 0) * mm, "end": v(-10.13, -2) * mm});
            skLineSegment(sketch, "E90", {"start": v(-90.13, -2) * mm, "end": v(-90.13, 0) * mm});
            skLineSegment(sketch, "E91", {"start": v(-90.13, 0) * mm, "end": v(-88.13, 0) * mm});
            skSolve(sketch);
        }
        {
            var Q0;
            Q0=makeQuery(id+"F14.imprint","IMPRINT",FACE,{"disambiguationData":[TD([[makeQuery(id+"F14.imprint","IMPRINT",EDGE,{"derivedFrom":sQuery(id+"F14.wireOp",EDGE,"E85")}),-1.0]])]});
            var Q1;
            Q1=makeQuery(id+"F14.imprint","IMPRINT",FACE,{"disambiguationData":[TD([[makeQuery(id+"F14.imprint","IMPRINT",EDGE,{"derivedFrom":sQuery(id+"F14.wireOp",EDGE,"E87.MirrorCS")}),1.0]])]});
            var Q2;
            Q2=makeQuery(id+"F9.opExtrude","SWEPT_FACE",FACE,{"disambiguationData":[OSD([sQuery(id+"F8.wireOp",EDGE,"E64.0.20.0")])]});
            extrude(context, id + "F15", {"entities" : qUnion([Q0, Q1]), "operationType" : NewBodyOperationType.REMOVE, "endBound" : BoundingType.UP_TO_SURFACE, "oppositeDirection" : true, "endBoundEntityFace" : qUnion([Q2]), "depth" : 25 * mm});
        }
        {
            var Q0;
            Q0=makeQuery(id+"F9.opExtrude","CAP_FACE",FACE,{"disambiguationData":[OSD([sQuery(id+"F8.wireOp",EDGE,"E60"),sQuery(id+"F8.wireOp",EDGE,"E62"),sQuery(id+"F8.wireOp",EDGE,"E63.0.20.0"),sQuery(id+"F8.wireOp",EDGE,"E64.0.20.0"),sQuery(id+"F8.wireOp",EDGE,"E65.bottom"),sQuery(id+"F8.wireOp",EDGE,"E65.top"),sQuery(id+"F8.wireOp",EDGE,"E65.left"),sQuery(id+"F8.wireOp",EDGE,"E65.right"),sQuery(id+"F8.wireOp",EDGE,"E66.bottom"),sQuery(id+"F8.wireOp",EDGE,"E66.top"),sQuery(id+"F8.wireOp",EDGE,"E66.left"),sQuery(id+"F8.wireOp",EDGE,"E66.right"),sQuery(id+"F8.wireOp",EDGE,"E67.bottom"),sQuery(id+"F8.wireOp",EDGE,"E67.top"),sQuery(id+"F8.wireOp",EDGE,"E67.left"),sQuery(id+"F8.wireOp",EDGE,"E67.right"),sQuery(id+"F8.wireOp",EDGE,"E68.bottom"),sQuery(id+"F8.wireOp",EDGE,"E68.left"),sQuery(id+"F8.wireOp",EDGE,"E68.right"),sQuery(id+"F8.wireOp",EDGE,"E69.bottom"),sQuery(id+"F8.wireOp",EDGE,"E69.top"),sQuery(id+"F8.wireOp",EDGE,"E69.left"),sQuery(id+"F8.wireOp",EDGE,"E69.right"),sQuery(id+"F8.wireOp",EDGE,"E70.bottom"),sQuery(id+"F8.wireOp",EDGE,"E70.left"),sQuery(id+"F8.wireOp",EDGE,"E70.right"),sQuery(id+"F8.wireOp",EDGE,"E71.bottom"),sQuery(id+"F8.wireOp",EDGE,"E71.top"),sQuery(id+"F8.wireOp",EDGE,"E71.left"),sQuery(id+"F8.wireOp",EDGE,"E71.right"),sQuery(id+"F8.wireOp",EDGE,"E72.bottom"),sQuery(id+"F8.wireOp",EDGE,"E72.top"),sQuery(id+"F8.wireOp",EDGE,"E72.left"),sQuery(id+"F8.wireOp",EDGE,"E72.right"),sQuery(id+"F8.wireOp",EDGE,"E73.bottom"),sQuery(id+"F8.wireOp",EDGE,"E73.top"),sQuery(id+"F8.wireOp",EDGE,"E73.left"),sQuery(id+"F8.wireOp",EDGE,"E73.right"),sQuery(id+"F8.wireOp",EDGE,"E74.bottom"),sQuery(id+"F8.wireOp",EDGE,"E74.top"),sQuery(id+"F8.wireOp",EDGE,"E74.left"),sQuery(id+"F8.wireOp",EDGE,"E74.right"),sQuery(id+"F8.wireOp",EDGE,"E75.bottom"),sQuery(id+"F8.wireOp",EDGE,"E75.left"),sQuery(id+"F8.wireOp",EDGE,"E75.right"),sQuery(id+"F8.wireOp",EDGE,"E76.bottom"),sQuery(id+"F8.wireOp",EDGE,"E76.top"),sQuery(id+"F8.wireOp",EDGE,"E76.left"),sQuery(id+"F8.wireOp",EDGE,"E76.right"),sQuery(id+"F8.wireOp",EDGE,"E77.top"),sQuery(id+"F8.wireOp",EDGE,"E77.left"),sQuery(id+"F8.wireOp",EDGE,"E77.right"),sQuery(id+"F8.wireOp",EDGE,"E78.bottom"),sQuery(id+"F8.wireOp",EDGE,"E78.top"),sQuery(id+"F8.wireOp",EDGE,"E78.left"),sQuery(id+"F8.wireOp",EDGE,"E78.right"),sQuery(id+"F8.wireOp",EDGE,"E79.bottom"),sQuery(id+"F8.wireOp",EDGE,"E79.top"),sQuery(id+"F8.wireOp",EDGE,"E79.left"),sQuery(id+"F8.wireOp",EDGE,"E79.right"),sQuery(id+"F8.wireOp",EDGE,"E80.bottom"),sQuery(id+"F8.wireOp",EDGE,"E80.left"),sQuery(id+"F8.wireOp",EDGE,"E80.right"),sQuery(id+"F8.wireOp",EDGE,"E81.bottom"),sQuery(id+"F8.wireOp",EDGE,"E81.top"),sQuery(id+"F8.wireOp",EDGE,"E81.left"),sQuery(id+"F8.wireOp",EDGE,"E81.right")])],"isStart":true});
            var sketch = newSketch(context, id + "F16", { "sketchPlane" : qUnion([Q0])});
            skLineSegment(sketch, "E92", {"start": v(20.13, 19.5) * mm, "end": v(20.13, 24.5) * mm});
            skLineSegment(sketch, "E93.1.0.0", {"start": v(25.13, 19.5) * mm, "end": v(25.13, 24.5) * mm});
            skLineSegment(sketch, "E93.2.0.0", {"start": v(30.13, 19.5) * mm, "end": v(30.13, 24.5) * mm});
            skLineSegment(sketch, "E93.3.0.0", {"start": v(35.13, 19.5) * mm, "end": v(35.13, 24.5) * mm});
            skLineSegment(sketch, "E93.4.0.0", {"start": v(40.13, 19.5) * mm, "end": v(40.13, 24.5) * mm});
            skLineSegment(sketch, "E93.5.0.0", {"start": v(45.13, 19.5) * mm, "end": v(45.13, 24.5) * mm});
            skLineSegment(sketch, "E93.6.0.0", {"start": v(50.13, 19.5) * mm, "end": v(50.13, 24.5) * mm});
            skLineSegment(sketch, "E93.7.0.0", {"start": v(55.13, 19.5) * mm, "end": v(55.13, 24.5) * mm});
            skLineSegment(sketch, "E93.8.0.0", {"start": v(60.13, 19.5) * mm, "end": v(60.13, 24.5) * mm});
            skLineSegment(sketch, "E93.9.0.0", {"start": v(65.13, 19.5) * mm, "end": v(65.13, 24.5) * mm});
            skLineSegment(sketch, "E93.10.0.0", {"start": v(70.13, 19.5) * mm, "end": v(70.13, 24.5) * mm});
            skLineSegment(sketch, "E93.11.0.0", {"start": v(75.13, 19.5) * mm, "end": v(75.13, 24.5) * mm});
            skLineSegment(sketch, "E93.12.0.0", {"start": v(80.13, 19.5) * mm, "end": v(80.13, 24.5) * mm});
            skLineSegment(sketch, "E93.direction1", {"start": v(20.13, 19.5) * mm, "end": v(25.13, 19.5) * mm, "construction": true});
            skLineSegment(sketch, "E94", {"start": v(20.13, 24.5) * mm, "end": v(80.13, 24.5) * mm});
            skLineSegment(sketch, "E95.bottom", {"start": v(20.18, 24.5) * mm, "end": v(25.08, 24.5) * mm});
            skLineSegment(sketch, "E95.top", {"start": v(20.18, 19.6) * mm, "end": v(25.08, 19.6) * mm});
            skLineSegment(sketch, "E95.left", {"start": v(20.18, 24.5) * mm, "end": v(20.18, 19.6) * mm});
            skLineSegment(sketch, "E95.right", {"start": v(25.08, 24.5) * mm, "end": v(25.08, 19.6) * mm});
            skLineSegment(sketch, "E96.1.0.0", {"start": v(25.18, 19.6) * mm, "end": v(30.08, 19.6) * mm});
            skLineSegment(sketch, "E96.1.0.1", {"start": v(30.08, 24.5) * mm, "end": v(30.08, 19.6) * mm});
            skLineSegment(sketch, "E96.1.0.2", {"start": v(25.18, 24.5) * mm, "end": v(30.08, 24.5) * mm});
            skLineSegment(sketch, "E96.1.0.3", {"start": v(25.18, 24.5) * mm, "end": v(25.18, 19.6) * mm});
            skLineSegment(sketch, "E96.2.0.0", {"start": v(30.18, 19.6) * mm, "end": v(35.08, 19.6) * mm});
            skLineSegment(sketch, "E96.2.0.1", {"start": v(35.08, 24.5) * mm, "end": v(35.08, 19.6) * mm});
            skLineSegment(sketch, "E96.2.0.2", {"start": v(30.18, 24.5) * mm, "end": v(35.08, 24.5) * mm});
            skLineSegment(sketch, "E96.2.0.3", {"start": v(30.18, 24.5) * mm, "end": v(30.18, 19.6) * mm});
            skLineSegment(sketch, "E96.3.0.0", {"start": v(35.18, 19.6) * mm, "end": v(40.08, 19.6) * mm});
            skLineSegment(sketch, "E96.3.0.1", {"start": v(40.08, 24.5) * mm, "end": v(40.08, 19.6) * mm});
            skLineSegment(sketch, "E96.3.0.2", {"start": v(35.18, 24.5) * mm, "end": v(40.08, 24.5) * mm});
            skLineSegment(sketch, "E96.3.0.3", {"start": v(35.18, 24.5) * mm, "end": v(35.18, 19.6) * mm});
            skLineSegment(sketch, "E96.4.0.0", {"start": v(40.18, 19.6) * mm, "end": v(45.08, 19.6) * mm});
            skLineSegment(sketch, "E96.4.0.1", {"start": v(45.08, 24.5) * mm, "end": v(45.08, 19.6) * mm});
            skLineSegment(sketch, "E96.4.0.2", {"start": v(40.18, 24.5) * mm, "end": v(45.08, 24.5) * mm});
            skLineSegment(sketch, "E96.4.0.3", {"start": v(40.18, 24.5) * mm, "end": v(40.18, 19.6) * mm});
            skLineSegment(sketch, "E96.5.0.0", {"start": v(45.18, 19.6) * mm, "end": v(50.08, 19.6) * mm});
            skLineSegment(sketch, "E96.5.0.1", {"start": v(50.08, 24.5) * mm, "end": v(50.08, 19.6) * mm});
            skLineSegment(sketch, "E96.5.0.2", {"start": v(45.18, 24.5) * mm, "end": v(50.08, 24.5) * mm});
            skLineSegment(sketch, "E96.5.0.3", {"start": v(45.18, 24.5) * mm, "end": v(45.18, 19.6) * mm});
            skLineSegment(sketch, "E96.6.0.0", {"start": v(50.18, 19.6) * mm, "end": v(55.08, 19.6) * mm});
            skLineSegment(sketch, "E96.6.0.1", {"start": v(55.08, 24.5) * mm, "end": v(55.08, 19.6) * mm});
            skLineSegment(sketch, "E96.6.0.2", {"start": v(50.18, 24.5) * mm, "end": v(55.08, 24.5) * mm});
            skLineSegment(sketch, "E96.6.0.3", {"start": v(50.18, 24.5) * mm, "end": v(50.18, 19.6) * mm});
            skLineSegment(sketch, "E96.7.0.0", {"start": v(55.18, 19.6) * mm, "end": v(60.08, 19.6) * mm});
            skLineSegment(sketch, "E96.7.0.1", {"start": v(60.08, 24.5) * mm, "end": v(60.08, 19.6) * mm});
            skLineSegment(sketch, "E96.7.0.2", {"start": v(55.18, 24.5) * mm, "end": v(60.08, 24.5) * mm});
            skLineSegment(sketch, "E96.7.0.3", {"start": v(55.18, 24.5) * mm, "end": v(55.18, 19.6) * mm});
            skLineSegment(sketch, "E96.8.0.0", {"start": v(60.18, 19.6) * mm, "end": v(65.08, 19.6) * mm});
            skLineSegment(sketch, "E96.8.0.1", {"start": v(65.08, 24.5) * mm, "end": v(65.08, 19.6) * mm});
            skLineSegment(sketch, "E96.8.0.2", {"start": v(60.18, 24.5) * mm, "end": v(65.08, 24.5) * mm});
            skLineSegment(sketch, "E96.8.0.3", {"start": v(60.18, 24.5) * mm, "end": v(60.18, 19.6) * mm});
            skLineSegment(sketch, "E96.9.0.0", {"start": v(65.18, 19.6) * mm, "end": v(70.08, 19.6) * mm});
            skLineSegment(sketch, "E96.9.0.1", {"start": v(70.08, 24.5) * mm, "end": v(70.08, 19.6) * mm});
            skLineSegment(sketch, "E96.9.0.2", {"start": v(65.18, 24.5) * mm, "end": v(70.08, 24.5) * mm});
            skLineSegment(sketch, "E96.9.0.3", {"start": v(65.18, 24.5) * mm, "end": v(65.18, 19.6) * mm});
            skLineSegment(sketch, "E96.10.0.0", {"start": v(70.18, 19.6) * mm, "end": v(75.08, 19.6) * mm});
            skLineSegment(sketch, "E96.10.0.1", {"start": v(75.08, 24.5) * mm, "end": v(75.08, 19.6) * mm});
            skLineSegment(sketch, "E96.10.0.2", {"start": v(70.18, 24.5) * mm, "end": v(75.08, 24.5) * mm});
            skLineSegment(sketch, "E96.10.0.3", {"start": v(70.18, 24.5) * mm, "end": v(70.18, 19.6) * mm});
            skLineSegment(sketch, "E96.11.0.0", {"start": v(75.18, 19.6) * mm, "end": v(80.08, 19.6) * mm});
            skLineSegment(sketch, "E96.11.0.1", {"start": v(80.08, 24.5) * mm, "end": v(80.08, 19.6) * mm});
            skLineSegment(sketch, "E96.11.0.2", {"start": v(75.18, 24.5) * mm, "end": v(80.08, 24.5) * mm});
            skLineSegment(sketch, "E96.11.0.3", {"start": v(75.18, 24.5) * mm, "end": v(75.18, 19.6) * mm});
            skLineSegment(sketch, "E96.direction1", {"start": v(20.18, 19.6) * mm, "end": v(25.18, 19.6) * mm, "construction": true});
            skLineSegment(sketch, "E97", {"start": v(21.63, 24.5) * mm, "end": v(21.63, 22.17) * mm});
            skLineSegment(sketch, "E98", {"start": v(21.63, 22.17) * mm, "end": v(23.63, 22.17) * mm});
            skLineSegment(sketch, "E99", {"start": v(23.63, 22.17) * mm, "end": v(23.63, 24.5) * mm});
            skLineSegment(sketch, "E100", {"start": v(22.63, 24.5) * mm, "end": v(22.63, 22.17) * mm, "construction": true});
            skLineSegment(sketch, "E101.1.0.0", {"start": v(28.63, 22.17) * mm, "end": v(28.63, 24.5) * mm});
            skLineSegment(sketch, "E101.1.0.1", {"start": v(26.63, 22.17) * mm, "end": v(28.63, 22.17) * mm});
            skLineSegment(sketch, "E101.1.0.2", {"start": v(26.63, 24.5) * mm, "end": v(26.63, 22.17) * mm});
            skLineSegment(sketch, "E101.2.0.0", {"start": v(33.63, 22.17) * mm, "end": v(33.63, 24.5) * mm});
            skLineSegment(sketch, "E101.2.0.1", {"start": v(31.63, 22.17) * mm, "end": v(33.63, 22.17) * mm});
            skLineSegment(sketch, "E101.2.0.2", {"start": v(31.63, 24.5) * mm, "end": v(31.63, 22.17) * mm});
            skLineSegment(sketch, "E101.3.0.0", {"start": v(38.63, 22.17) * mm, "end": v(38.63, 24.5) * mm});
            skLineSegment(sketch, "E101.3.0.1", {"start": v(36.63, 22.17) * mm, "end": v(38.63, 22.17) * mm});
            skLineSegment(sketch, "E101.3.0.2", {"start": v(36.63, 24.5) * mm, "end": v(36.63, 22.17) * mm});
            skLineSegment(sketch, "E101.4.0.0", {"start": v(43.63, 22.17) * mm, "end": v(43.63, 24.5) * mm});
            skLineSegment(sketch, "E101.4.0.1", {"start": v(41.63, 22.17) * mm, "end": v(43.63, 22.17) * mm});
            skLineSegment(sketch, "E101.4.0.2", {"start": v(41.63, 24.5) * mm, "end": v(41.63, 22.17) * mm});
            skLineSegment(sketch, "E101.5.0.0", {"start": v(48.63, 22.17) * mm, "end": v(48.63, 24.5) * mm});
            skLineSegment(sketch, "E101.5.0.1", {"start": v(46.63, 22.17) * mm, "end": v(48.63, 22.17) * mm});
            skLineSegment(sketch, "E101.5.0.2", {"start": v(46.63, 24.5) * mm, "end": v(46.63, 22.17) * mm});
            skLineSegment(sketch, "E101.6.0.0", {"start": v(53.63, 22.17) * mm, "end": v(53.63, 24.5) * mm});
            skLineSegment(sketch, "E101.6.0.1", {"start": v(51.63, 22.17) * mm, "end": v(53.63, 22.17) * mm});
            skLineSegment(sketch, "E101.6.0.2", {"start": v(51.63, 24.5) * mm, "end": v(51.63, 22.17) * mm});
            skLineSegment(sketch, "E101.7.0.0", {"start": v(58.63, 22.17) * mm, "end": v(58.63, 24.5) * mm});
            skLineSegment(sketch, "E101.7.0.1", {"start": v(56.63, 22.17) * mm, "end": v(58.63, 22.17) * mm});
            skLineSegment(sketch, "E101.7.0.2", {"start": v(56.63, 24.5) * mm, "end": v(56.63, 22.17) * mm});
            skLineSegment(sketch, "E101.8.0.0", {"start": v(63.63, 22.17) * mm, "end": v(63.63, 24.5) * mm});
            skLineSegment(sketch, "E101.8.0.1", {"start": v(61.63, 22.17) * mm, "end": v(63.63, 22.17) * mm});
            skLineSegment(sketch, "E101.8.0.2", {"start": v(61.63, 24.5) * mm, "end": v(61.63, 22.17) * mm});
            skLineSegment(sketch, "E101.9.0.0", {"start": v(68.63, 22.17) * mm, "end": v(68.63, 24.5) * mm});
            skLineSegment(sketch, "E101.9.0.1", {"start": v(66.63, 22.17) * mm, "end": v(68.63, 22.17) * mm});
            skLineSegment(sketch, "E101.9.0.2", {"start": v(66.63, 24.5) * mm, "end": v(66.63, 22.17) * mm});
            skLineSegment(sketch, "E101.10.0.0", {"start": v(73.63, 22.17) * mm, "end": v(73.63, 24.5) * mm});
            skLineSegment(sketch, "E101.10.0.1", {"start": v(71.63, 22.17) * mm, "end": v(73.63, 22.17) * mm});
            skLineSegment(sketch, "E101.10.0.2", {"start": v(71.63, 24.5) * mm, "end": v(71.63, 22.17) * mm});
            skLineSegment(sketch, "E101.11.0.0", {"start": v(78.63, 22.17) * mm, "end": v(78.63, 24.5) * mm});
            skLineSegment(sketch, "E101.11.0.1", {"start": v(76.63, 22.17) * mm, "end": v(78.63, 22.17) * mm});
            skLineSegment(sketch, "E101.11.0.2", {"start": v(76.63, 24.5) * mm, "end": v(76.63, 22.17) * mm});
            skLineSegment(sketch, "E101.direction1", {"start": v(23.63, 22.17) * mm, "end": v(28.63, 22.17) * mm, "construction": true});
            skSolve(sketch);
        }
        {
            var Q0;
            Q0=makeQuery(id+"F16.imprint","IMPRINT",FACE,{"disambiguationData":[TD([[makeQuery(id+"F16.imprint","IMPRINT",EDGE,{"derivedFrom":sQuery(id+"F16.wireOp",EDGE,"E95.bottom")}),-1.0]])]});
            var Q1;
            Q1=makeQuery(id+"F16.imprint","IMPRINT",FACE,{"disambiguationData":[TD([[makeQuery(id+"F16.imprint","IMPRINT",EDGE,{"derivedFrom":sQuery(id+"F16.wireOp",EDGE,"E96.2.0.0")}),1.0]])]});
            var Q2;
            Q2=makeQuery(id+"F16.imprint","IMPRINT",FACE,{"disambiguationData":[TD([[makeQuery(id+"F16.imprint","IMPRINT",EDGE,{"derivedFrom":sQuery(id+"F16.wireOp",EDGE,"E96.4.0.0")}),1.0]])]});
            var Q3;
            Q3=makeQuery(id+"F16.imprint","IMPRINT",FACE,{"disambiguationData":[TD([[makeQuery(id+"F16.imprint","IMPRINT",EDGE,{"derivedFrom":sQuery(id+"F16.wireOp",EDGE,"E96.7.0.0")}),1.0]])]});
            var Q4;
            Q4=makeQuery(id+"F16.imprint","IMPRINT",FACE,{"disambiguationData":[TD([[makeQuery(id+"F16.imprint","IMPRINT",EDGE,{"derivedFrom":sQuery(id+"F16.wireOp",EDGE,"E96.9.0.0")}),1.0]])]});
            var Q5;
            Q5=makeQuery(id+"F16.imprint","IMPRINT",FACE,{"disambiguationData":[TD([[makeQuery(id+"F16.imprint","IMPRINT",EDGE,{"derivedFrom":sQuery(id+"F16.wireOp",EDGE,"E96.11.0.0")}),1.0]])]});
            extrude(context, id + "F17", {"entities" : qUnion([Q0, Q1, Q2, Q3, Q4, Q5]), "operationType" : NewBodyOperationType.ADD, "depth" : 5 * mm});
        }
        {
            var Q0;
            Q0=makeQuery(id+"F9.opExtrude","CAP_FACE",FACE,{"disambiguationData":[OSD([sQuery(id+"F8.wireOp",EDGE,"E60"),sQuery(id+"F8.wireOp",EDGE,"E62"),sQuery(id+"F8.wireOp",EDGE,"E63.0.20.0"),sQuery(id+"F8.wireOp",EDGE,"E64.0.20.0"),sQuery(id+"F8.wireOp",EDGE,"E65.bottom"),sQuery(id+"F8.wireOp",EDGE,"E65.top"),sQuery(id+"F8.wireOp",EDGE,"E65.left"),sQuery(id+"F8.wireOp",EDGE,"E65.right"),sQuery(id+"F8.wireOp",EDGE,"E66.bottom"),sQuery(id+"F8.wireOp",EDGE,"E66.top"),sQuery(id+"F8.wireOp",EDGE,"E66.left"),sQuery(id+"F8.wireOp",EDGE,"E66.right"),sQuery(id+"F8.wireOp",EDGE,"E67.bottom"),sQuery(id+"F8.wireOp",EDGE,"E67.top"),sQuery(id+"F8.wireOp",EDGE,"E67.left"),sQuery(id+"F8.wireOp",EDGE,"E67.right"),sQuery(id+"F8.wireOp",EDGE,"E68.bottom"),sQuery(id+"F8.wireOp",EDGE,"E68.left"),sQuery(id+"F8.wireOp",EDGE,"E68.right"),sQuery(id+"F8.wireOp",EDGE,"E69.bottom"),sQuery(id+"F8.wireOp",EDGE,"E69.top"),sQuery(id+"F8.wireOp",EDGE,"E69.left"),sQuery(id+"F8.wireOp",EDGE,"E69.right"),sQuery(id+"F8.wireOp",EDGE,"E70.bottom"),sQuery(id+"F8.wireOp",EDGE,"E70.left"),sQuery(id+"F8.wireOp",EDGE,"E70.right"),sQuery(id+"F8.wireOp",EDGE,"E71.bottom"),sQuery(id+"F8.wireOp",EDGE,"E71.top"),sQuery(id+"F8.wireOp",EDGE,"E71.left"),sQuery(id+"F8.wireOp",EDGE,"E71.right"),sQuery(id+"F8.wireOp",EDGE,"E72.bottom"),sQuery(id+"F8.wireOp",EDGE,"E72.top"),sQuery(id+"F8.wireOp",EDGE,"E72.left"),sQuery(id+"F8.wireOp",EDGE,"E72.right"),sQuery(id+"F8.wireOp",EDGE,"E73.bottom"),sQuery(id+"F8.wireOp",EDGE,"E73.top"),sQuery(id+"F8.wireOp",EDGE,"E73.left"),sQuery(id+"F8.wireOp",EDGE,"E73.right"),sQuery(id+"F8.wireOp",EDGE,"E74.bottom"),sQuery(id+"F8.wireOp",EDGE,"E74.top"),sQuery(id+"F8.wireOp",EDGE,"E74.left"),sQuery(id+"F8.wireOp",EDGE,"E74.right"),sQuery(id+"F8.wireOp",EDGE,"E75.bottom"),sQuery(id+"F8.wireOp",EDGE,"E75.left"),sQuery(id+"F8.wireOp",EDGE,"E75.right"),sQuery(id+"F8.wireOp",EDGE,"E76.bottom"),sQuery(id+"F8.wireOp",EDGE,"E76.top"),sQuery(id+"F8.wireOp",EDGE,"E76.left"),sQuery(id+"F8.wireOp",EDGE,"E76.right"),sQuery(id+"F8.wireOp",EDGE,"E77.top"),sQuery(id+"F8.wireOp",EDGE,"E77.left"),sQuery(id+"F8.wireOp",EDGE,"E77.right"),sQuery(id+"F8.wireOp",EDGE,"E78.bottom"),sQuery(id+"F8.wireOp",EDGE,"E78.top"),sQuery(id+"F8.wireOp",EDGE,"E78.left"),sQuery(id+"F8.wireOp",EDGE,"E78.right"),sQuery(id+"F8.wireOp",EDGE,"E79.bottom"),sQuery(id+"F8.wireOp",EDGE,"E79.top"),sQuery(id+"F8.wireOp",EDGE,"E79.left"),sQuery(id+"F8.wireOp",EDGE,"E79.right"),sQuery(id+"F8.wireOp",EDGE,"E80.bottom"),sQuery(id+"F8.wireOp",EDGE,"E80.left"),sQuery(id+"F8.wireOp",EDGE,"E80.right"),sQuery(id+"F8.wireOp",EDGE,"E81.bottom"),sQuery(id+"F8.wireOp",EDGE,"E81.top"),sQuery(id+"F8.wireOp",EDGE,"E81.left"),sQuery(id+"F8.wireOp",EDGE,"E81.right")])],"isStart":true});
            var sketch = newSketch(context, id + "F18", { "sketchPlane" : qUnion([Q0])});
            skLineSegment(sketch, "E102", {"start": v(21.68, 24.5) * mm, "end": v(21.68, 22.27) * mm});
            skPoint(sketch, "E102.startSnap0", {"position": v(20.9, 24.5) * mm});
            skLineSegment(sketch, "E103", {"start": v(21.68, 22.27) * mm, "end": v(23.58, 22.27) * mm});
            skLineSegment(sketch, "E104", {"start": v(23.58, 22.27) * mm, "end": v(23.58, 24.5) * mm});
            skLineSegment(sketch, "E105.1.0.0", {"start": v(28.58, 22.27) * mm, "end": v(28.58, 24.5) * mm});
            skLineSegment(sketch, "E105.1.0.1", {"start": v(26.68, 22.27) * mm, "end": v(28.58, 22.27) * mm});
            skLineSegment(sketch, "E105.1.0.2", {"start": v(26.68, 24.5) * mm, "end": v(26.68, 22.27) * mm});
            skLineSegment(sketch, "E105.2.0.0", {"start": v(33.58, 22.27) * mm, "end": v(33.58, 24.5) * mm});
            skLineSegment(sketch, "E105.2.0.1", {"start": v(31.68, 22.27) * mm, "end": v(33.58, 22.27) * mm});
            skLineSegment(sketch, "E105.2.0.2", {"start": v(31.68, 24.5) * mm, "end": v(31.68, 22.27) * mm});
            skLineSegment(sketch, "E105.3.0.0", {"start": v(38.58, 22.27) * mm, "end": v(38.58, 24.5) * mm});
            skLineSegment(sketch, "E105.3.0.1", {"start": v(36.68, 22.27) * mm, "end": v(38.58, 22.27) * mm});
            skLineSegment(sketch, "E105.3.0.2", {"start": v(36.68, 24.5) * mm, "end": v(36.68, 22.27) * mm});
            skLineSegment(sketch, "E105.4.0.0", {"start": v(43.58, 22.27) * mm, "end": v(43.58, 24.5) * mm});
            skLineSegment(sketch, "E105.4.0.1", {"start": v(41.68, 22.27) * mm, "end": v(43.58, 22.27) * mm});
            skLineSegment(sketch, "E105.4.0.2", {"start": v(41.68, 24.5) * mm, "end": v(41.68, 22.27) * mm});
            skLineSegment(sketch, "E105.5.0.0", {"start": v(48.58, 22.27) * mm, "end": v(48.58, 24.5) * mm});
            skLineSegment(sketch, "E105.5.0.1", {"start": v(46.68, 22.27) * mm, "end": v(48.58, 22.27) * mm});
            skLineSegment(sketch, "E105.5.0.2", {"start": v(46.68, 24.5) * mm, "end": v(46.68, 22.27) * mm});
            skLineSegment(sketch, "E105.6.0.0", {"start": v(53.58, 22.27) * mm, "end": v(53.58, 24.5) * mm});
            skLineSegment(sketch, "E105.6.0.1", {"start": v(51.68, 22.27) * mm, "end": v(53.58, 22.27) * mm});
            skLineSegment(sketch, "E105.6.0.2", {"start": v(51.68, 24.5) * mm, "end": v(51.68, 22.27) * mm});
            skLineSegment(sketch, "E105.7.0.0", {"start": v(58.58, 22.27) * mm, "end": v(58.58, 24.5) * mm});
            skLineSegment(sketch, "E105.7.0.1", {"start": v(56.68, 22.27) * mm, "end": v(58.58, 22.27) * mm});
            skLineSegment(sketch, "E105.7.0.2", {"start": v(56.68, 24.5) * mm, "end": v(56.68, 22.27) * mm});
            skLineSegment(sketch, "E105.8.0.0", {"start": v(63.58, 22.27) * mm, "end": v(63.58, 24.5) * mm});
            skLineSegment(sketch, "E105.8.0.1", {"start": v(61.68, 22.27) * mm, "end": v(63.58, 22.27) * mm});
            skLineSegment(sketch, "E105.8.0.2", {"start": v(61.68, 24.5) * mm, "end": v(61.68, 22.27) * mm});
            skLineSegment(sketch, "E105.9.0.0", {"start": v(68.58, 22.27) * mm, "end": v(68.58, 24.5) * mm});
            skLineSegment(sketch, "E105.9.0.1", {"start": v(66.68, 22.27) * mm, "end": v(68.58, 22.27) * mm});
            skLineSegment(sketch, "E105.9.0.2", {"start": v(66.68, 24.5) * mm, "end": v(66.68, 22.27) * mm});
            skLineSegment(sketch, "E105.10.0.0", {"start": v(73.58, 22.27) * mm, "end": v(73.58, 24.5) * mm});
            skLineSegment(sketch, "E105.10.0.1", {"start": v(71.68, 22.27) * mm, "end": v(73.58, 22.27) * mm});
            skLineSegment(sketch, "E105.10.0.2", {"start": v(71.68, 24.5) * mm, "end": v(71.68, 22.27) * mm});
            skLineSegment(sketch, "E105.11.0.0", {"start": v(78.58, 22.27) * mm, "end": v(78.58, 24.5) * mm});
            skLineSegment(sketch, "E105.11.0.1", {"start": v(76.68, 22.27) * mm, "end": v(78.58, 22.27) * mm});
            skLineSegment(sketch, "E105.11.0.2", {"start": v(76.68, 24.5) * mm, "end": v(76.68, 22.27) * mm});
            skLineSegment(sketch, "E105.direction1", {"start": v(23.58, 22.27) * mm, "end": v(28.58, 22.27) * mm, "construction": true});
            skLineSegment(sketch, "E106", {"start": v(12.13, 24.5) * mm, "end": v(12.13, 24.5) * mm});
            skLineSegment(sketch, "E107", {"start": v(12.13, 24.5) * mm, "end": v(88.13, 24.5) * mm});
            skLineSegment(sketch, "E108", {"start": v(88.13, 24.5) * mm, "end": v(88.13, 97.5) * mm});
            skLineSegment(sketch, "E109", {"start": v(12.13, 24.5) * mm, "end": v(12.13, 97.5) * mm});
            skLineSegment(sketch, "E110.0", {"start": v(88.13, 97.5) * mm, "end": v(12.13, 97.5) * mm});
            skSolve(sketch);
        }
        {
            var Q0;
            Q0=makeQuery(id+"F18.imprint","IMPRINT",FACE,{"disambiguationData":[TD([[makeQuery(id+"F18.imprint","IMPRINT",EDGE,{"derivedFrom":makeQuery(id+"F9.opExtrude","CAP_EDGE",EDGE,{"disambiguationData":[OSD([sQuery(id+"F8.wireOp",EDGE,"E66.bottom")])],"isStart":true})}),1.0]])]});
            var Q1;
            Q1=makeQuery(id+"F18.imprint","IMPRINT",FACE,{"disambiguationData":[TD([[makeQuery(id+"F18.imprint","IMPRINT",EDGE,{"derivedFrom":makeQuery(id+"F9.opExtrude","CAP_EDGE",EDGE,{"disambiguationData":[OSD([sQuery(id+"F8.wireOp",EDGE,"E74.bottom")])],"isStart":true})}),1.0]])]});
            var Q2;
            Q2=makeQuery(id+"F18.imprint","IMPRINT",FACE,{"disambiguationData":[TD([[makeQuery(id+"F18.imprint","IMPRINT",EDGE,{"derivedFrom":makeQuery(id+"F9.opExtrude","CAP_EDGE",EDGE,{"disambiguationData":[OSD([sQuery(id+"F8.wireOp",EDGE,"E68.bottom")])],"isStart":true})}),1.0]])]});
            var Q3;
            Q3=makeQuery(id+"F18.imprint","IMPRINT",FACE,{"disambiguationData":[TD([[makeQuery(id+"F18.imprint","IMPRINT",EDGE,{"derivedFrom":makeQuery(id+"F9.opExtrude","CAP_EDGE",EDGE,{"disambiguationData":[OSD([sQuery(id+"F8.wireOp",EDGE,"E73.bottom")])],"isStart":true})}),-1.0]])]});
            var Q4;
            Q4=makeQuery(id+"F18.imprint","IMPRINT",FACE,{"disambiguationData":[TD([[makeQuery(id+"F18.imprint","IMPRINT",EDGE,{"derivedFrom":makeQuery(id+"F9.opExtrude","CAP_EDGE",EDGE,{"disambiguationData":[OSD([sQuery(id+"F8.wireOp",EDGE,"E81.bottom")])],"isStart":true})}),-1.0]])]});
            var Q5;
            Q5=makeQuery(id+"F18.imprint","IMPRINT",FACE,{"disambiguationData":[TD([[makeQuery(id+"F18.imprint","IMPRINT",EDGE,{"derivedFrom":makeQuery(id+"F9.opExtrude","CAP_EDGE",EDGE,{"disambiguationData":[OSD([sQuery(id+"F8.wireOp",EDGE,"E65.bottom")])],"isStart":true})}),1.0]])]});
            var Q6;
            Q6=makeQuery(id+"F18.imprint","IMPRINT",FACE,{"disambiguationData":[TD([[makeQuery(id+"F18.imprint","IMPRINT",EDGE,{"derivedFrom":makeQuery(id+"F9.opExtrude","CAP_EDGE",EDGE,{"disambiguationData":[OSD([sQuery(id+"F8.wireOp",EDGE,"E67.bottom")])],"isStart":true})}),-1.0]])]});
            var Q7;
            {var subQ28=sQuery(id+"F18.wireOp",EDGE,"E108");Q7=makeQuery(id+"F18.imprint","IMPRINT",FACE,{"disambiguationData":[TD([[makeQuery(id+"F18.imprint","IMPRINT",EDGE,{"derivedFrom":subQ28}),1.0]])]});}
            var Q8;
            Q8=makeQuery(id+"F18.imprint","IMPRINT",FACE,{"disambiguationData":[TD([[makeQuery(id+"F18.imprint","IMPRINT",EDGE,{"derivedFrom":makeQuery(id+"F9.opExtrude","CAP_EDGE",EDGE,{"disambiguationData":[OSD([sQuery(id+"F8.wireOp",EDGE,"E70.bottom")])],"isStart":true})}),1.0]])]});
            var Q9;
            Q9=makeQuery(id+"F18.imprint","IMPRINT",FACE,{"disambiguationData":[TD([[makeQuery(id+"F18.imprint","IMPRINT",EDGE,{"derivedFrom":makeQuery(id+"F9.opExtrude","CAP_EDGE",EDGE,{"disambiguationData":[OSD([sQuery(id+"F8.wireOp",EDGE,"E75.bottom")])],"isStart":true})}),1.0]])]});
            var Q10;
            Q10=makeQuery(id+"F18.imprint","IMPRINT",FACE,{"disambiguationData":[TD([[makeQuery(id+"F18.imprint","IMPRINT",EDGE,{"derivedFrom":makeQuery(id+"F9.opExtrude","CAP_EDGE",EDGE,{"disambiguationData":[OSD([sQuery(id+"F8.wireOp",EDGE,"E79.bottom")])],"isStart":true})}),-1.0]])]});
            var Q11;
            Q11=makeQuery(id+"F18.imprint","IMPRINT",FACE,{"disambiguationData":[TD([[makeQuery(id+"F18.imprint","IMPRINT",EDGE,{"derivedFrom":makeQuery(id+"F9.opExtrude","CAP_EDGE",EDGE,{"disambiguationData":[OSD([sQuery(id+"F8.wireOp",EDGE,"E78.bottom")])],"isStart":true})}),-1.0]])]});
            var Q12;
            Q12=makeQuery(id+"F18.imprint","IMPRINT",FACE,{"disambiguationData":[TD([[makeQuery(id+"F18.imprint","IMPRINT",EDGE,{"derivedFrom":makeQuery(id+"F9.opExtrude","CAP_EDGE",EDGE,{"disambiguationData":[OSD([sQuery(id+"F8.wireOp",EDGE,"E72.bottom")])],"isStart":true})}),1.0]])]});
            var Q13;
            {var subQ0=sQuery(id+"F18.wireOp",EDGE,"E105.4.0.0");Q13=makeQuery(id+"F18.imprint","IMPRINT",FACE,{"disambiguationData":[TD([[makeQuery(id+"F18.imprint","IMPRINT",EDGE,{"derivedFrom":subQ0}),1.0]])]});}
            var Q14;
            {var subQ0=sQuery(id+"F18.wireOp",EDGE,"E105.9.0.0");Q14=makeQuery(id+"F18.imprint","IMPRINT",FACE,{"disambiguationData":[TD([[makeQuery(id+"F18.imprint","IMPRINT",EDGE,{"derivedFrom":subQ0}),1.0]])]});}
            var Q15;
            {var subQ0=sQuery(id+"F18.wireOp",EDGE,"E105.11.0.0");Q15=makeQuery(id+"F18.imprint","IMPRINT",FACE,{"disambiguationData":[TD([[makeQuery(id+"F18.imprint","IMPRINT",EDGE,{"derivedFrom":subQ0}),1.0]])]});}
            var Q16;
            {var subQ0=sQuery(id+"F18.wireOp",EDGE,"E105.2.0.0");Q16=makeQuery(id+"F18.imprint","IMPRINT",FACE,{"disambiguationData":[TD([[makeQuery(id+"F18.imprint","IMPRINT",EDGE,{"derivedFrom":subQ0}),1.0]])]});}
            var Q17;
            {var subQ0=sQuery(id+"F18.wireOp",EDGE,"E105.7.0.0");Q17=makeQuery(id+"F18.imprint","IMPRINT",FACE,{"disambiguationData":[TD([[makeQuery(id+"F18.imprint","IMPRINT",EDGE,{"derivedFrom":subQ0}),1.0]])]});}
            var Q18;
            {var subQ0=sQuery(id+"F18.wireOp",EDGE,"E102");Q18=makeQuery(id+"F18.imprint","IMPRINT",FACE,{"disambiguationData":[TD([[makeQuery(id+"F18.imprint","IMPRINT",EDGE,{"derivedFrom":subQ0}),1.0]])]});}
            extrude(context, id + "F19", {"entities" : qUnion([Q0, Q1, Q2, Q3, Q4, Q5, Q6, Q7, Q8, Q9, Q10, Q11, Q12, Q13, Q14, Q15, Q16, Q17, Q18]), "depth" : 2 * mm});
        }
        {
            var Q0;
            Q0=makeQuery(id+"F19.opExtrude","SWEPT_FACE",FACE,{"disambiguationData":[OSD([sQuery(id+"F18.wireOp",EDGE,"E110.0")])]});
            var sketch = newSketch(context, id + "F20", { "sketchPlane" : qUnion([Q0])});
            skLineSegment(sketch, "E111", {"start": v(-88.13, 0) * mm, "end": v(-86.13, 2) * mm});
            skLineSegment(sketch, "E112", {"start": v(-12.13, 0) * mm, "end": v(-14.13, 2) * mm});
            skLineSegment(sketch, "E113", {"start": v(-12.13, 0) * mm, "end": v(-12.13, 2) * mm});
            skLineSegment(sketch, "E114", {"start": v(-12.13, 2) * mm, "end": v(-14.13, 2) * mm});
            skLineSegment(sketch, "E115", {"start": v(-86.13, 2) * mm, "end": v(-88.13, 2) * mm});
            skLineSegment(sketch, "E116", {"start": v(-88.13, 2) * mm, "end": v(-88.13, 0) * mm});
            skSolve(sketch);
        }
        {
            var Q0;
            {var subQ0=sQuery(id+"F20.wireOp",EDGE,"E112");Q0=makeQuery(id+"F20.imprint","IMPRINT",FACE,{"disambiguationData":[TD([[makeQuery(id+"F20.imprint","IMPRINT",EDGE,{"derivedFrom":subQ0}),-1.0]])]});}
            var Q1;
            {var subQ0=sQuery(id+"F20.wireOp",EDGE,"E111");Q1=makeQuery(id+"F20.imprint","IMPRINT",FACE,{"disambiguationData":[TD([[makeQuery(id+"F20.imprint","IMPRINT",EDGE,{"derivedFrom":subQ0}),1.0]])]});}
            extrude(context, id + "F21", {"entities" : qUnion([Q0, Q1]), "operationType" : NewBodyOperationType.REMOVE, "endBound" : BoundingType.UP_TO_NEXT, "oppositeDirection" : true, "depth" : 25 * mm});
        }
        {
            var Q0;
            {var subQ0=sQuery(id+"F18.wireOp",EDGE,"E102");Q0=makeQuery(id+"F18.imprint","IMPRINT",FACE,{"disambiguationData":[TD([[makeQuery(id+"F18.imprint","IMPRINT",EDGE,{"derivedFrom":subQ0}),1.0]])]});}
            var Q1;
            {var subQ3=sQuery(id+"F18.wireOp",EDGE,"E105.2.0.0");Q1=makeQuery(id+"F18.imprint","IMPRINT",FACE,{"disambiguationData":[TD([[makeQuery(id+"F18.imprint","IMPRINT",EDGE,{"derivedFrom":subQ3}),-1.0]])]});}
            var Q2;
            {var subQ0=sQuery(id+"F18.wireOp",EDGE,"E105.2.0.0");Q2=makeQuery(id+"F18.imprint","IMPRINT",FACE,{"disambiguationData":[TD([[makeQuery(id+"F18.imprint","IMPRINT",EDGE,{"derivedFrom":subQ0}),1.0]])]});}
            var Q3;
            {var subQ0=sQuery(id+"F18.wireOp",EDGE,"E105.4.0.0");Q3=makeQuery(id+"F18.imprint","IMPRINT",FACE,{"disambiguationData":[TD([[makeQuery(id+"F18.imprint","IMPRINT",EDGE,{"derivedFrom":subQ0}),1.0]])]});}
            var Q4;
            {var subQ0=sQuery(id+"F18.wireOp",EDGE,"E105.11.0.0");Q4=makeQuery(id+"F18.imprint","IMPRINT",FACE,{"disambiguationData":[TD([[makeQuery(id+"F18.imprint","IMPRINT",EDGE,{"derivedFrom":subQ0}),1.0]])]});}
            var Q5;
            {var subQ0=sQuery(id+"F18.wireOp",EDGE,"E105.9.0.0");Q5=makeQuery(id+"F18.imprint","IMPRINT",FACE,{"disambiguationData":[TD([[makeQuery(id+"F18.imprint","IMPRINT",EDGE,{"derivedFrom":subQ0}),1.0]])]});}
            var Q6;
            {var subQ0=sQuery(id+"F18.wireOp",EDGE,"E105.7.0.0");Q6=makeQuery(id+"F18.imprint","IMPRINT",FACE,{"disambiguationData":[TD([[makeQuery(id+"F18.imprint","IMPRINT",EDGE,{"derivedFrom":subQ0}),1.0]])]});}
            extrude(context, id + "F22", {"entities" : qUnion([Q0, Q1, Q2, Q3, Q4, Q5, Q6]), "operationType" : NewBodyOperationType.ADD, "depth" : 5 * mm});
        }
        {
            var Q0;
            Q0=qCreatedBy(makeId("Top.planeOp"),FACE);
            cPlane(context, id + "F23", {"entities" : qUnion([Q0]), "cplaneType" : CPlaneType.OFFSET, "offset" : 130 * mm, "width" : 150 * mm, "height" : 150 * mm});
        }
        {
            var Q0;
            Q0=qCreatedBy(id+"F23.planeOp",FACE);
            var sketch = newSketch(context, id + "F24", { "sketchPlane" : qUnion([Q0])});
            skLineSegment(sketch, "E117.bottom", {"start": v(35.98, -35.97) * mm, "end": v(-35.98, -35.98) * mm});
            skLineSegment(sketch, "E117.top", {"start": v(35.98, 35.98) * mm, "end": v(-35.97, 35.98) * mm});
            skLineSegment(sketch, "E117.left", {"start": v(35.98, -35.98) * mm, "end": v(35.98, 35.98) * mm});
            skLineSegment(sketch, "E117.right", {"start": v(-35.98, -35.98) * mm, "end": v(-35.98, 35.97) * mm});
            skPoint(sketch, "E117.middle", {"position": v(0, 0) * mm});
            skSolve(sketch);
        }
        {
            var Q0;
            Q0=makeQuery(id+"F24.imprint","IMPRINT",FACE,{"disambiguationData":[TD([[makeQuery(id+"F24.imprint","IMPRINT",EDGE,{"derivedFrom":sQuery(id+"F24.wireOp",EDGE,"E117.bottom")}),-1.0]])]});
            extrude(context, id + "F25", {"entities" : qUnion([Q0]), "depth" : 2 * mm});
        }
    });
